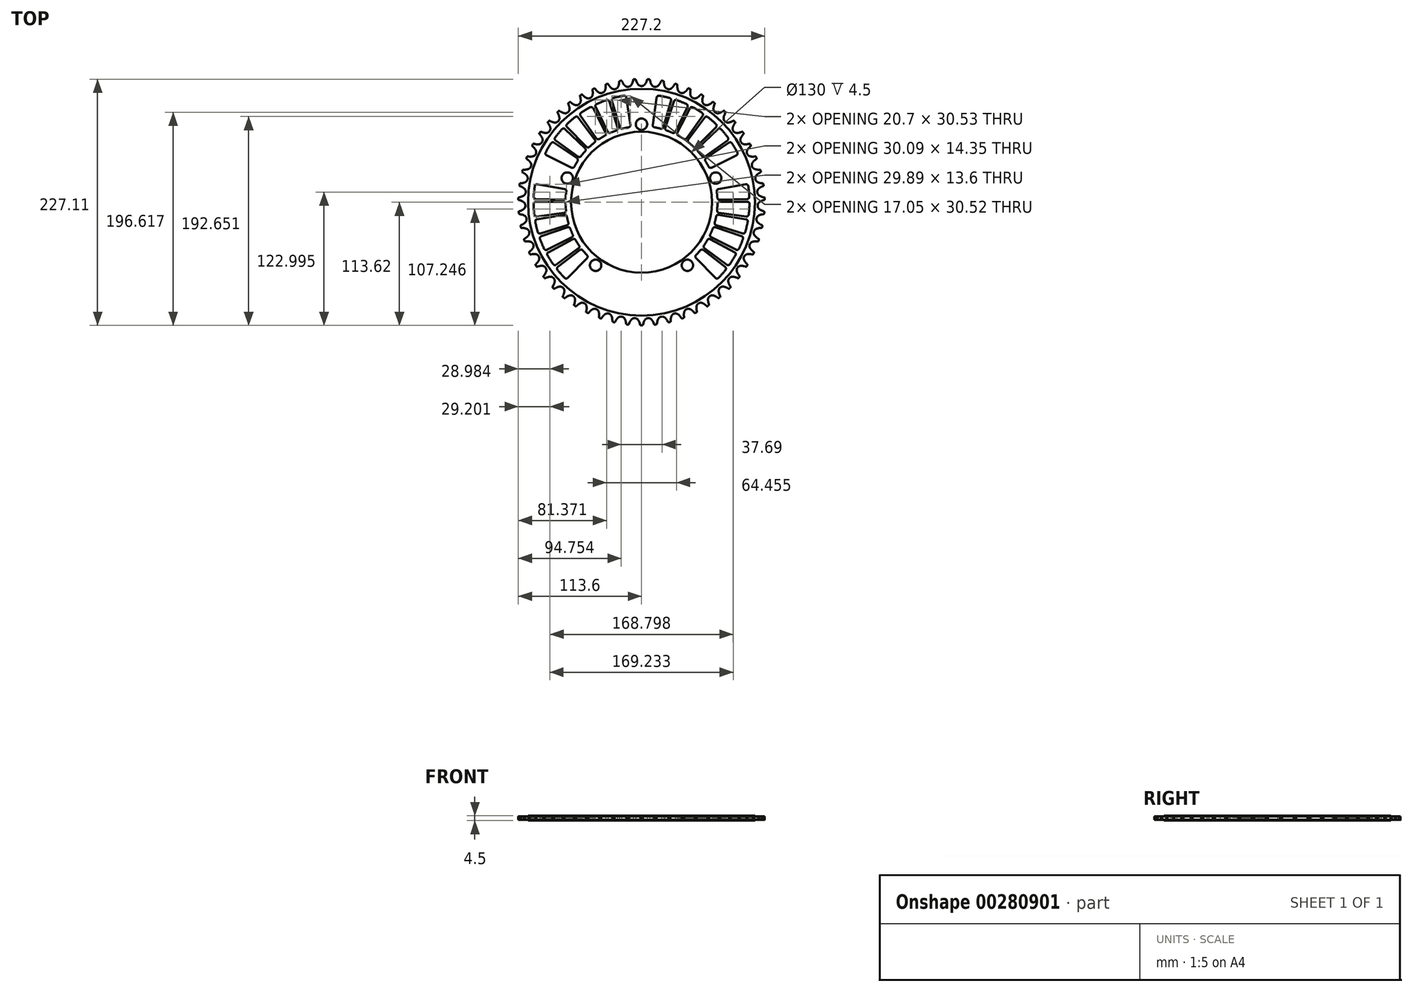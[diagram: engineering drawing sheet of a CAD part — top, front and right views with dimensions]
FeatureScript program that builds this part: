
annotation { "Feature Type Name" : "Feature", "Feature Type Description" : "" }
export const myFeature = defineFeature(function(context is Context, id is Id, definition is map)
    precondition{}
    {
        {
            var Q0;
            Q0=qCreatedBy(makeId("Top.planeOp"),FACE);
            var sketch = newSketch(context, id + "F0", { "sketchPlane" : qUnion([Q0])});
            skCircle(sketch, "E0", {"center": v(0, 0) * mm, "radius": 111.17 * mm, "construction": true});
            skArc(sketch, "E1", {"start": v(-4.68, 111.51) * mm, "mid": v(-4.06, 110.1) * mm, "end": v(-3.24, 108.8) * mm});
            skLineSegment(sketch, "E2", {"start": v(-4.68, 111.51) * mm, "end": v(-5.07, 112.63) * mm});
            skArc(sketch, "E3.trimOffspring", {"start": v(-5.07, 112.63) * mm, "mid": v(-5.69, 113.92) * mm, "end": v(-6.58, 115.05) * mm});
            skArc(sketch, "E4.trimOffspring", {"start": v(-3.24, 108.8) * mm, "mid": v(-1.82, 107.6) * mm, "end": v(0, 107.15) * mm});
            skArc(sketch, "E5.MirrorCS", {"start": v(3.24, 108.8) * mm, "mid": v(1.82, 107.6) * mm, "end": v(0, 107.15) * mm});
            skArc(sketch, "E6.MirrorCS", {"start": v(4.68, 111.51) * mm, "mid": v(4.06, 110.1) * mm, "end": v(3.24, 108.8) * mm});
            skLineSegment(sketch, "E7.MirrorCS", {"start": v(4.68, 111.51) * mm, "end": v(5.07, 112.63) * mm});
            skArc(sketch, "E8.MirrorCS", {"start": v(5.07, 112.63) * mm, "mid": v(5.69, 113.92) * mm, "end": v(6.58, 115.05) * mm});
            skArc(sketch, "E9.1.0", {"start": v(-15.63, 107.73) * mm, "mid": v(-14.07, 106.68) * mm, "end": v(-12.21, 106.46) * mm});
            skArc(sketch, "E9.1.1", {"start": v(-9.18, 108.47) * mm, "mid": v(-10.46, 107.1) * mm, "end": v(-12.21, 106.46) * mm});
            skArc(sketch, "E9.1.2", {"start": v(-8.06, 111.32) * mm, "mid": v(-8.51, 109.85) * mm, "end": v(-9.18, 108.47) * mm});
            skArc(sketch, "E9.1.3", {"start": v(-17.36, 110.25) * mm, "mid": v(-16.59, 108.93) * mm, "end": v(-15.63, 107.73) * mm});
            skArc(sketch, "E9.1.4", {"start": v(-7.8, 112.47) * mm, "mid": v(-7.34, 113.83) * mm, "end": v(-6.58, 115.05) * mm});
            skArc(sketch, "E9.1.5", {"start": v(-17.87, 111.32) * mm, "mid": v(-18.64, 112.53) * mm, "end": v(-19.65, 113.55) * mm});
            skLineSegment(sketch, "E9.1.6", {"start": v(-8.06, 111.32) * mm, "end": v(-7.8, 112.47) * mm});
            skLineSegment(sketch, "E9.1.7", {"start": v(-17.36, 110.25) * mm, "end": v(-17.87, 111.32) * mm});
            skArc(sketch, "E9.2.0", {"start": v(-27.8, 105.24) * mm, "mid": v(-26.14, 104.38) * mm, "end": v(-24.27, 104.37) * mm});
            skArc(sketch, "E9.2.1", {"start": v(-21.48, 106.71) * mm, "mid": v(-22.6, 105.2) * mm, "end": v(-24.27, 104.37) * mm});
            skArc(sketch, "E9.2.2", {"start": v(-20.7, 109.68) * mm, "mid": v(-20.98, 108.16) * mm, "end": v(-21.48, 106.71) * mm});
            skArc(sketch, "E9.2.3", {"start": v(-29.82, 107.56) * mm, "mid": v(-28.9, 106.32) * mm, "end": v(-27.8, 105.24) * mm});
            skArc(sketch, "E9.2.4", {"start": v(-20.57, 110.85) * mm, "mid": v(-20.26, 112.25) * mm, "end": v(-19.65, 113.55) * mm});
            skArc(sketch, "E9.2.5", {"start": v(-30.45, 108.55) * mm, "mid": v(-31.34, 109.68) * mm, "end": v(-32.47, 110.57) * mm});
            skLineSegment(sketch, "E9.2.6", {"start": v(-20.7, 109.68) * mm, "end": v(-20.57, 110.85) * mm});
            skLineSegment(sketch, "E9.2.7", {"start": v(-29.82, 107.56) * mm, "end": v(-30.45, 108.55) * mm});
            skArc(sketch, "E9.3.0", {"start": v(-39.62, 101.39) * mm, "mid": v(-37.87, 100.72) * mm, "end": v(-36, 100.92) * mm});
            skArc(sketch, "E9.3.1", {"start": v(-33.5, 103.57) * mm, "mid": v(-34.44, 101.95) * mm, "end": v(-36, 100.92) * mm});
            skArc(sketch, "E9.3.2", {"start": v(-33.07, 106.6) * mm, "mid": v(-33.17, 105.07) * mm, "end": v(-33.5, 103.57) * mm});
            skArc(sketch, "E9.3.3", {"start": v(-41.88, 103.46) * mm, "mid": v(-40.83, 102.34) * mm, "end": v(-39.62, 101.39) * mm});
            skArc(sketch, "E9.3.4", {"start": v(-33.08, 107.78) * mm, "mid": v(-32.93, 109.2) * mm, "end": v(-32.47, 110.57) * mm});
            skArc(sketch, "E9.3.5", {"start": v(-42.62, 104.38) * mm, "mid": v(-43.64, 105.39) * mm, "end": v(-44.86, 106.15) * mm});
            skLineSegment(sketch, "E9.3.6", {"start": v(-33.07, 106.6) * mm, "end": v(-33.08, 107.78) * mm});
            skLineSegment(sketch, "E9.3.7", {"start": v(-41.88, 103.46) * mm, "end": v(-42.62, 104.38) * mm});
            skArc(sketch, "E9.4.0", {"start": v(-50.92, 96.2) * mm, "mid": v(-49.1, 95.75) * mm, "end": v(-47.28, 96.16) * mm});
            skArc(sketch, "E9.4.1", {"start": v(-45.1, 99.07) * mm, "mid": v(-45.84, 97.35) * mm, "end": v(-47.28, 96.16) * mm});
            skArc(sketch, "E9.4.2", {"start": v(-45, 102.14) * mm, "mid": v(-44.93, 100.6) * mm, "end": v(-45.1, 99.07) * mm});
            skArc(sketch, "E9.4.3", {"start": v(-53.4, 98) * mm, "mid": v(-52.23, 97.02) * mm, "end": v(-50.92, 96.2) * mm});
            skArc(sketch, "E9.4.4", {"start": v(-45.15, 103.3) * mm, "mid": v(-45.16, 104.74) * mm, "end": v(-44.86, 106.15) * mm});
            skArc(sketch, "E9.4.5", {"start": v(-54.24, 98.84) * mm, "mid": v(-55.37, 99.73) * mm, "end": v(-56.67, 100.34) * mm});
            skLineSegment(sketch, "E9.4.6", {"start": v(-45, 102.14) * mm, "end": v(-45.15, 103.3) * mm});
            skLineSegment(sketch, "E9.4.7", {"start": v(-53.4, 98) * mm, "end": v(-54.24, 98.84) * mm});
            skArc(sketch, "E9.5.0", {"start": v(-61.55, 89.78) * mm, "mid": v(-59.7, 89.53) * mm, "end": v(-57.93, 90.14) * mm});
            skArc(sketch, "E9.5.1", {"start": v(-56.1, 93.29) * mm, "mid": v(-56.64, 91.5) * mm, "end": v(-57.93, 90.14) * mm});
            skArc(sketch, "E9.5.2", {"start": v(-56.35, 96.34) * mm, "mid": v(-56.1, 94.82) * mm, "end": v(-56.1, 93.29) * mm});
            skArc(sketch, "E9.5.3", {"start": v(-64.23, 91.28) * mm, "mid": v(-62.95, 90.43) * mm, "end": v(-61.55, 89.78) * mm});
            skArc(sketch, "E9.5.4", {"start": v(-56.63, 97.49) * mm, "mid": v(-56.8, 98.91) * mm, "end": v(-56.67, 100.34) * mm});
            skArc(sketch, "E9.5.5", {"start": v(-65.15, 92) * mm, "mid": v(-66.38, 92.76) * mm, "end": v(-67.73, 93.23) * mm});
            skLineSegment(sketch, "E9.5.6", {"start": v(-56.35, 96.34) * mm, "end": v(-56.63, 97.49) * mm});
            skLineSegment(sketch, "E9.5.7", {"start": v(-64.23, 91.28) * mm, "end": v(-65.15, 92) * mm});
            skArc(sketch, "E9.6.0", {"start": v(-71.39, 82.18) * mm, "mid": v(-69.52, 82.14) * mm, "end": v(-67.83, 82.95) * mm});
            skArc(sketch, "E9.6.1", {"start": v(-66.36, 86.28) * mm, "mid": v(-66.7, 84.44) * mm, "end": v(-67.83, 82.95) * mm});
            skArc(sketch, "E9.6.2", {"start": v(-66.97, 89.3) * mm, "mid": v(-66.55, 87.8) * mm, "end": v(-66.36, 86.28) * mm});
            skArc(sketch, "E9.6.3", {"start": v(-74.21, 83.36) * mm, "mid": v(-72.84, 82.67) * mm, "end": v(-71.39, 82.18) * mm});
            skArc(sketch, "E9.6.4", {"start": v(-67.37, 90.4) * mm, "mid": v(-67.71, 91.8) * mm, "end": v(-67.73, 93.23) * mm});
            skArc(sketch, "E9.6.5", {"start": v(-75.22, 83.98) * mm, "mid": v(-76.52, 84.6) * mm, "end": v(-77.92, 84.9) * mm});
            skLineSegment(sketch, "E9.6.6", {"start": v(-66.97, 89.3) * mm, "end": v(-67.37, 90.4) * mm});
            skLineSegment(sketch, "E9.6.7", {"start": v(-74.21, 83.36) * mm, "end": v(-75.22, 83.98) * mm});
            skArc(sketch, "E9.7.0", {"start": v(-80.29, 73.5) * mm, "mid": v(-78.43, 73.68) * mm, "end": v(-76.84, 74.68) * mm});
            skArc(sketch, "E9.7.1", {"start": v(-75.77, 78.16) * mm, "mid": v(-75.89, 76.29) * mm, "end": v(-76.84, 74.68) * mm});
            skArc(sketch, "E9.7.2", {"start": v(-76.7, 81.08) * mm, "mid": v(-76.13, 79.65) * mm, "end": v(-75.77, 78.16) * mm});
            skArc(sketch, "E9.7.3", {"start": v(-83.23, 74.36) * mm, "mid": v(-81.8, 73.82) * mm, "end": v(-80.29, 73.5) * mm});
            skArc(sketch, "E9.7.4", {"start": v(-77.24, 82.13) * mm, "mid": v(-77.74, 83.48) * mm, "end": v(-77.92, 84.9) * mm});
            skArc(sketch, "E9.7.5", {"start": v(-84.3, 74.86) * mm, "mid": v(-85.66, 75.32) * mm, "end": v(-87.09, 75.46) * mm});
            skLineSegment(sketch, "E9.7.6", {"start": v(-76.7, 81.08) * mm, "end": v(-77.24, 82.13) * mm});
            skLineSegment(sketch, "E9.7.7", {"start": v(-83.23, 74.36) * mm, "end": v(-84.3, 74.86) * mm});
            skArc(sketch, "E9.8.0", {"start": v(-88.14, 63.87) * mm, "mid": v(-86.31, 64.26) * mm, "end": v(-84.86, 65.43) * mm});
            skArc(sketch, "E9.8.1", {"start": v(-84.18, 69.01) * mm, "mid": v(-84.09, 67.14) * mm, "end": v(-84.86, 65.43) * mm});
            skArc(sketch, "E9.8.2", {"start": v(-85.45, 71.8) * mm, "mid": v(-84.71, 70.45) * mm, "end": v(-84.18, 69.01) * mm});
            skArc(sketch, "E9.8.3", {"start": v(-91.17, 64.39) * mm, "mid": v(-89.67, 64.02) * mm, "end": v(-88.14, 63.87) * mm});
            skArc(sketch, "E9.8.4", {"start": v(-86.1, 72.79) * mm, "mid": v(-86.74, 74.07) * mm, "end": v(-87.09, 75.46) * mm});
            skArc(sketch, "E9.8.5", {"start": v(-92.29, 64.76) * mm, "mid": v(-93.69, 65.06) * mm, "end": v(-95.12, 65.04) * mm});
            skLineSegment(sketch, "E9.8.6", {"start": v(-85.45, 71.8) * mm, "end": v(-86.1, 72.79) * mm});
            skLineSegment(sketch, "E9.8.7", {"start": v(-91.17, 64.39) * mm, "end": v(-92.29, 64.76) * mm});
            skArc(sketch, "E9.9.0", {"start": v(-94.85, 53.4) * mm, "mid": v(-93.08, 54) * mm, "end": v(-91.76, 55.33) * mm});
            skArc(sketch, "E9.9.1", {"start": v(-91.5, 58.96) * mm, "mid": v(-91.2, 57.12) * mm, "end": v(-91.76, 55.33) * mm});
            skArc(sketch, "E9.9.2", {"start": v(-93.08, 61.6) * mm, "mid": v(-92.2, 60.34) * mm, "end": v(-91.5, 58.96) * mm});
            skArc(sketch, "E9.9.3", {"start": v(-97.91, 53.58) * mm, "mid": v(-96.39, 53.38) * mm, "end": v(-94.85, 53.4) * mm});
            skArc(sketch, "E9.9.4", {"start": v(-93.83, 62.5) * mm, "mid": v(-94.62, 63.7) * mm, "end": v(-95.12, 65.04) * mm});
            skArc(sketch, "E9.9.5", {"start": v(-99.07, 53.82) * mm, "mid": v(-100.5, 53.96) * mm, "end": v(-101.92, 53.78) * mm});
            skLineSegment(sketch, "E9.9.6", {"start": v(-93.08, 61.6) * mm, "end": v(-93.83, 62.5) * mm});
            skLineSegment(sketch, "E9.9.7", {"start": v(-97.91, 53.58) * mm, "end": v(-99.07, 53.82) * mm});
            skArc(sketch, "E9.10.0", {"start": v(-100.32, 42.25) * mm, "mid": v(-98.62, 43.04) * mm, "end": v(-97.47, 44.51) * mm});
            skArc(sketch, "E9.10.1", {"start": v(-97.62, 48.15) * mm, "mid": v(-97.11, 46.35) * mm, "end": v(-97.47, 44.51) * mm});
            skArc(sketch, "E9.10.2", {"start": v(-99.5, 50.58) * mm, "mid": v(-98.47, 49.44) * mm, "end": v(-97.62, 48.15) * mm});
            skArc(sketch, "E9.10.3", {"start": v(-103.38, 42.07) * mm, "mid": v(-101.84, 42.04) * mm, "end": v(-100.32, 42.25) * mm});
            skArc(sketch, "E9.10.4", {"start": v(-100.35, 51.4) * mm, "mid": v(-101.27, 52.5) * mm, "end": v(-101.92, 53.78) * mm});
            skArc(sketch, "E9.10.5", {"start": v(-104.56, 42.18) * mm, "mid": v(-106, 42.15) * mm, "end": v(-107.38, 41.8) * mm});
            skLineSegment(sketch, "E9.10.6", {"start": v(-99.5, 50.58) * mm, "end": v(-100.35, 51.4) * mm});
            skLineSegment(sketch, "E9.10.7", {"start": v(-103.38, 42.07) * mm, "end": v(-104.56, 42.18) * mm});
            skArc(sketch, "E9.11.0", {"start": v(-104.48, 30.54) * mm, "mid": v(-102.89, 31.52) * mm, "end": v(-101.91, 33.11) * mm});
            skArc(sketch, "E9.11.1", {"start": v(-102.48, 36.7) * mm, "mid": v(-101.76, 34.98) * mm, "end": v(-101.91, 33.11) * mm});
            skArc(sketch, "E9.11.2", {"start": v(-104.6, 38.91) * mm, "mid": v(-103.46, 37.89) * mm, "end": v(-102.48, 36.7) * mm});
            skArc(sketch, "E9.11.3", {"start": v(-107.5, 30) * mm, "mid": v(-105.97, 30.16) * mm, "end": v(-104.48, 30.54) * mm});
            skArc(sketch, "E9.11.4", {"start": v(-105.55, 39.62) * mm, "mid": v(-106.6, 40.61) * mm, "end": v(-107.38, 41.8) * mm});
            skArc(sketch, "E9.11.5", {"start": v(-108.68, 29.98) * mm, "mid": v(-110.1, 29.8) * mm, "end": v(-111.45, 29.3) * mm});
            skLineSegment(sketch, "E9.11.6", {"start": v(-104.6, 38.91) * mm, "end": v(-105.55, 39.62) * mm});
            skLineSegment(sketch, "E9.11.7", {"start": v(-107.5, 30) * mm, "end": v(-108.68, 29.98) * mm});
            skArc(sketch, "E9.12.0", {"start": v(-107.28, 18.43) * mm, "mid": v(-105.8, 19.58) * mm, "end": v(-105.02, 21.28) * mm});
            skArc(sketch, "E9.12.1", {"start": v(-106, 24.79) * mm, "mid": v(-105.09, 23.15) * mm, "end": v(-105.02, 21.28) * mm});
            skArc(sketch, "E9.12.2", {"start": v(-108.36, 26.73) * mm, "mid": v(-107.1, 25.85) * mm, "end": v(-106, 24.79) * mm});
            skArc(sketch, "E9.12.3", {"start": v(-110.22, 17.56) * mm, "mid": v(-108.72, 17.88) * mm, "end": v(-107.28, 18.43) * mm});
            skArc(sketch, "E9.12.4", {"start": v(-109.38, 27.33) * mm, "mid": v(-110.53, 28.2) * mm, "end": v(-111.45, 29.3) * mm});
            skArc(sketch, "E9.12.5", {"start": v(-111.4, 17.4) * mm, "mid": v(-112.78, 17.05) * mm, "end": v(-114.06, 16.4) * mm});
            skLineSegment(sketch, "E9.12.6", {"start": v(-108.36, 26.73) * mm, "end": v(-109.38, 27.33) * mm});
            skLineSegment(sketch, "E9.12.7", {"start": v(-110.22, 17.56) * mm, "end": v(-111.4, 17.4) * mm});
            skArc(sketch, "E9.13.0", {"start": v(-108.68, 6.08) * mm, "mid": v(-107.35, 7.4) * mm, "end": v(-106.76, 9.17) * mm});
            skArc(sketch, "E9.13.1", {"start": v(-108.13, 12.54) * mm, "mid": v(-107.04, 11.02) * mm, "end": v(-106.76, 9.17) * mm});
            skArc(sketch, "E9.13.2", {"start": v(-110.7, 14.2) * mm, "mid": v(-109.35, 13.47) * mm, "end": v(-108.13, 12.54) * mm});
            skArc(sketch, "E9.13.3", {"start": v(-111.5, 4.88) * mm, "mid": v(-110.05, 5.37) * mm, "end": v(-108.68, 6.08) * mm});
            skArc(sketch, "E9.13.4", {"start": v(-111.78, 14.69) * mm, "mid": v(-113.02, 15.41) * mm, "end": v(-114.06, 16.4) * mm});
            skArc(sketch, "E9.13.5", {"start": v(-112.65, 4.59) * mm, "mid": v(-114, 4.08) * mm, "end": v(-115.19, 3.3) * mm});
            skLineSegment(sketch, "E9.13.6", {"start": v(-110.7, 14.2) * mm, "end": v(-111.78, 14.69) * mm});
            skLineSegment(sketch, "E9.13.7", {"start": v(-111.5, 4.88) * mm, "end": v(-112.65, 4.59) * mm});
            skArc(sketch, "E9.14.0", {"start": v(-108.67, -6.35) * mm, "mid": v(-107.5, -4.9) * mm, "end": v(-107.11, -3.06) * mm});
            skArc(sketch, "E9.14.1", {"start": v(-108.85, 0.14) * mm, "mid": v(-107.6, -1.25) * mm, "end": v(-107.11, -3.06) * mm});
            skArc(sketch, "E9.14.2", {"start": v(-111.6, 1.5) * mm, "mid": v(-110.18, 0.92) * mm, "end": v(-108.85, 0.14) * mm});
            skArc(sketch, "E9.14.3", {"start": v(-111.33, -7.86) * mm, "mid": v(-109.94, -7.2) * mm, "end": v(-108.67, -6.35) * mm});
            skArc(sketch, "E9.14.4", {"start": v(-112.73, 1.85) * mm, "mid": v(-114.04, 2.43) * mm, "end": v(-115.19, 3.3) * mm});
            skArc(sketch, "E9.14.5", {"start": v(-112.44, -8.28) * mm, "mid": v(-113.71, -8.94) * mm, "end": v(-114.81, -9.86) * mm});
            skLineSegment(sketch, "E9.14.6", {"start": v(-111.6, 1.5) * mm, "end": v(-112.73, 1.85) * mm});
            skLineSegment(sketch, "E9.14.7", {"start": v(-111.33, -7.86) * mm, "end": v(-112.44, -8.28) * mm});
            skArc(sketch, "E9.15.0", {"start": v(-107.24, -18.7) * mm, "mid": v(-106.24, -17.11) * mm, "end": v(-106.06, -15.25) * mm});
            skArc(sketch, "E9.15.1", {"start": v(-108.16, -12.27) * mm, "mid": v(-106.75, -13.51) * mm, "end": v(-106.06, -15.25) * mm});
            skArc(sketch, "E9.15.2", {"start": v(-111.05, -11.24) * mm, "mid": v(-109.56, -11.65) * mm, "end": v(-108.16, -12.27) * mm});
            skArc(sketch, "E9.15.3", {"start": v(-109.71, -20.5) * mm, "mid": v(-108.4, -19.7) * mm, "end": v(-107.24, -18.7) * mm});
            skArc(sketch, "E9.15.4", {"start": v(-112.2, -11.01) * mm, "mid": v(-113.57, -10.58) * mm, "end": v(-114.81, -9.86) * mm});
            skArc(sketch, "E9.15.5", {"start": v(-110.76, -21.04) * mm, "mid": v(-111.95, -21.84) * mm, "end": v(-112.94, -22.88) * mm});
            skLineSegment(sketch, "E9.15.6", {"start": v(-111.05, -11.24) * mm, "end": v(-112.2, -11.01) * mm});
            skLineSegment(sketch, "E9.15.7", {"start": v(-109.71, -20.5) * mm, "end": v(-110.76, -21.04) * mm});
            skArc(sketch, "E9.16.0", {"start": v(-104.4, -30.8) * mm, "mid": v(-103.6, -29.11) * mm, "end": v(-103.63, -27.24) * mm});
            skArc(sketch, "E9.16.1", {"start": v(-106.05, -24.52) * mm, "mid": v(-104.52, -25.6) * mm, "end": v(-103.63, -27.24) * mm});
            skArc(sketch, "E9.16.2", {"start": v(-109.04, -23.82) * mm, "mid": v(-107.52, -24.06) * mm, "end": v(-106.05, -24.52) * mm});
            skArc(sketch, "E9.16.3", {"start": v(-106.66, -32.88) * mm, "mid": v(-105.46, -31.92) * mm, "end": v(-104.4, -30.8) * mm});
            skArc(sketch, "E9.16.4", {"start": v(-110.22, -23.73) * mm, "mid": v(-111.63, -23.46) * mm, "end": v(-112.94, -22.88) * mm});
            skArc(sketch, "E9.16.5", {"start": v(-107.64, -33.53) * mm, "mid": v(-108.74, -34.46) * mm, "end": v(-109.6, -35.6) * mm});
            skLineSegment(sketch, "E9.16.6", {"start": v(-109.04, -23.82) * mm, "end": v(-110.22, -23.73) * mm});
            skLineSegment(sketch, "E9.16.7", {"start": v(-106.66, -32.88) * mm, "end": v(-107.64, -33.53) * mm});
            skArc(sketch, "E9.17.0", {"start": v(-100.21, -42.5) * mm, "mid": v(-99.6, -40.73) * mm, "end": v(-99.85, -38.88) * mm});
            skArc(sketch, "E9.17.1", {"start": v(-102.57, -36.45) * mm, "mid": v(-100.92, -37.34) * mm, "end": v(-99.85, -38.88) * mm});
            skArc(sketch, "E9.17.2", {"start": v(-105.61, -36.1) * mm, "mid": v(-104.08, -36.16) * mm, "end": v(-102.57, -36.45) * mm});
            skArc(sketch, "E9.17.3", {"start": v(-102.22, -44.82) * mm, "mid": v(-101.13, -43.73) * mm, "end": v(-100.21, -42.5) * mm});
            skArc(sketch, "E9.17.4", {"start": v(-106.8, -36.14) * mm, "mid": v(-108.22, -36.03) * mm, "end": v(-109.6, -35.6) * mm});
            skArc(sketch, "E9.17.5", {"start": v(-103.12, -45.58) * mm, "mid": v(-104.1, -46.63) * mm, "end": v(-104.82, -47.87) * mm});
            skLineSegment(sketch, "E9.17.6", {"start": v(-105.61, -36.1) * mm, "end": v(-106.8, -36.14) * mm});
            skLineSegment(sketch, "E9.17.7", {"start": v(-102.22, -44.82) * mm, "end": v(-103.12, -45.58) * mm});
            skArc(sketch, "E9.18.0", {"start": v(-94.72, -53.65) * mm, "mid": v(-94.3, -51.82) * mm, "end": v(-94.77, -50) * mm});
            skArc(sketch, "E9.18.1", {"start": v(-97.74, -47.9) * mm, "mid": v(-96, -48.6) * mm, "end": v(-94.77, -50) * mm});
            skArc(sketch, "E9.18.2", {"start": v(-100.81, -47.9) * mm, "mid": v(-99.28, -47.79) * mm, "end": v(-97.74, -47.9) * mm});
            skArc(sketch, "E9.18.3", {"start": v(-96.44, -56.18) * mm, "mid": v(-95.49, -54.98) * mm, "end": v(-94.72, -53.65) * mm});
            skArc(sketch, "E9.18.4", {"start": v(-101.98, -48.08) * mm, "mid": v(-103.41, -48.14) * mm, "end": v(-104.82, -47.87) * mm});
            skArc(sketch, "E9.18.5", {"start": v(-97.25, -57.04) * mm, "mid": v(-98.1, -58.2) * mm, "end": v(-98.68, -59.5) * mm});
            skLineSegment(sketch, "E9.18.6", {"start": v(-100.81, -47.9) * mm, "end": v(-101.98, -48.08) * mm});
            skLineSegment(sketch, "E9.18.7", {"start": v(-96.44, -56.18) * mm, "end": v(-97.25, -57.04) * mm});
            skArc(sketch, "E9.19.0", {"start": v(-87.98, -64.1) * mm, "mid": v(-87.79, -62.23) * mm, "end": v(-88.45, -60.48) * mm});
            skArc(sketch, "E9.19.1", {"start": v(-91.65, -58.74) * mm, "mid": v(-89.84, -59.23) * mm, "end": v(-88.45, -60.48) * mm});
            skArc(sketch, "E9.19.2", {"start": v(-94.7, -59.08) * mm, "mid": v(-93.18, -58.8) * mm, "end": v(-91.65, -58.74) * mm});
            skArc(sketch, "E9.19.3", {"start": v(-89.4, -66.8) * mm, "mid": v(-88.6, -65.5) * mm, "end": v(-87.98, -64.1) * mm});
            skArc(sketch, "E9.19.4", {"start": v(-95.83, -59.39) * mm, "mid": v(-97.25, -59.6) * mm, "end": v(-98.68, -59.5) * mm});
            skArc(sketch, "E9.19.5", {"start": v(-90.11, -67.76) * mm, "mid": v(-90.83, -69) * mm, "end": v(-91.26, -70.37) * mm});
            skLineSegment(sketch, "E9.19.6", {"start": v(-94.7, -59.08) * mm, "end": v(-95.83, -59.39) * mm});
            skLineSegment(sketch, "E9.19.7", {"start": v(-89.4, -66.8) * mm, "end": v(-90.11, -67.76) * mm});
            skArc(sketch, "E9.20.0", {"start": v(-80.1, -73.7) * mm, "mid": v(-80.12, -71.83) * mm, "end": v(-80.98, -70.17) * mm});
            skArc(sketch, "E9.20.1", {"start": v(-84.35, -68.8) * mm, "mid": v(-82.5, -69.08) * mm, "end": v(-80.98, -70.17) * mm});
            skArc(sketch, "E9.20.2", {"start": v(-87.34, -69.49) * mm, "mid": v(-85.87, -69.03) * mm, "end": v(-84.35, -68.8) * mm});
            skArc(sketch, "E9.20.3", {"start": v(-81.21, -76.56) * mm, "mid": v(-80.55, -75.17) * mm, "end": v(-80.1, -73.7) * mm});
            skArc(sketch, "E9.20.4", {"start": v(-88.44, -69.93) * mm, "mid": v(-89.82, -70.3) * mm, "end": v(-91.26, -70.37) * mm});
            skArc(sketch, "E9.20.5", {"start": v(-81.8, -77.59) * mm, "mid": v(-82.37, -78.9) * mm, "end": v(-82.64, -80.31) * mm});
            skLineSegment(sketch, "E9.20.6", {"start": v(-87.34, -69.49) * mm, "end": v(-88.44, -69.93) * mm});
            skLineSegment(sketch, "E9.20.7", {"start": v(-81.21, -76.56) * mm, "end": v(-81.8, -77.59) * mm});
            skArc(sketch, "E9.21.0", {"start": v(-71.18, -82.35) * mm, "mid": v(-71.4, -80.5) * mm, "end": v(-72.46, -78.95) * mm});
            skArc(sketch, "E9.21.1", {"start": v(-75.96, -77.97) * mm, "mid": v(-74.1, -78.04) * mm, "end": v(-72.46, -78.95) * mm});
            skArc(sketch, "E9.21.2", {"start": v(-78.85, -79) * mm, "mid": v(-77.44, -78.37) * mm, "end": v(-75.96, -77.97) * mm});
            skArc(sketch, "E9.21.3", {"start": v(-71.95, -85.32) * mm, "mid": v(-71.46, -83.87) * mm, "end": v(-71.18, -82.35) * mm});
            skArc(sketch, "E9.21.4", {"start": v(-79.89, -79.55) * mm, "mid": v(-81.22, -80.09) * mm, "end": v(-82.64, -80.31) * mm});
            skArc(sketch, "E9.21.5", {"start": v(-72.42, -86.4) * mm, "mid": v(-72.84, -87.78) * mm, "end": v(-72.95, -89.2) * mm});
            skLineSegment(sketch, "E9.21.6", {"start": v(-78.85, -79) * mm, "end": v(-79.89, -79.55) * mm});
            skLineSegment(sketch, "E9.21.7", {"start": v(-71.95, -85.32) * mm, "end": v(-72.42, -86.4) * mm});
            skArc(sketch, "E9.22.0", {"start": v(-61.33, -89.93) * mm, "mid": v(-61.77, -88.11) * mm, "end": v(-62.98, -86.69) * mm});
            skArc(sketch, "E9.22.1", {"start": v(-66.58, -86.12) * mm, "mid": v(-64.71, -85.97) * mm, "end": v(-62.98, -86.69) * mm});
            skArc(sketch, "E9.22.2", {"start": v(-69.33, -87.47) * mm, "mid": v(-68, -86.69) * mm, "end": v(-66.58, -86.12) * mm});
            skArc(sketch, "E9.22.3", {"start": v(-61.76, -92.97) * mm, "mid": v(-61.43, -91.47) * mm, "end": v(-61.33, -89.93) * mm});
            skArc(sketch, "E9.22.4", {"start": v(-70.3, -88.14) * mm, "mid": v(-71.56, -88.82) * mm, "end": v(-72.95, -89.2) * mm});
            skArc(sketch, "E9.22.5", {"start": v(-62.1, -94.1) * mm, "mid": v(-62.36, -95.5) * mm, "end": v(-62.3, -96.94) * mm});
            skLineSegment(sketch, "E9.22.6", {"start": v(-69.33, -87.47) * mm, "end": v(-70.3, -88.14) * mm});
            skLineSegment(sketch, "E9.22.7", {"start": v(-61.76, -92.97) * mm, "end": v(-62.1, -94.1) * mm});
            skArc(sketch, "E9.23.0", {"start": v(-50.68, -96.34) * mm, "mid": v(-51.32, -94.58) * mm, "end": v(-52.7, -93.3) * mm});
            skArc(sketch, "E9.23.1", {"start": v(-56.33, -93.15) * mm, "mid": v(-54.5, -92.79) * mm, "end": v(-52.7, -93.3) * mm});
            skArc(sketch, "E9.23.2", {"start": v(-58.91, -94.8) * mm, "mid": v(-57.68, -93.88) * mm, "end": v(-56.33, -93.15) * mm});
            skArc(sketch, "E9.23.3", {"start": v(-50.76, -99.4) * mm, "mid": v(-50.6, -97.87) * mm, "end": v(-50.68, -96.34) * mm});
            skArc(sketch, "E9.23.4", {"start": v(-59.8, -95.58) * mm, "mid": v(-60.97, -96.4) * mm, "end": v(-62.3, -96.94) * mm});
            skArc(sketch, "E9.23.5", {"start": v(-50.97, -100.56) * mm, "mid": v(-51.07, -102) * mm, "end": v(-50.84, -103.41) * mm});
            skLineSegment(sketch, "E9.23.6", {"start": v(-58.91, -94.8) * mm, "end": v(-59.8, -95.58) * mm});
            skLineSegment(sketch, "E9.23.7", {"start": v(-50.76, -99.4) * mm, "end": v(-50.97, -100.56) * mm});
            skArc(sketch, "E9.24.0", {"start": v(-39.37, -101.49) * mm, "mid": v(-40.2, -99.81) * mm, "end": v(-41.71, -98.7) * mm});
            skArc(sketch, "E9.24.1", {"start": v(-45.34, -98.96) * mm, "mid": v(-43.56, -98.4) * mm, "end": v(-41.71, -98.7) * mm});
            skArc(sketch, "E9.24.2", {"start": v(-47.72, -100.9) * mm, "mid": v(-46.6, -99.84) * mm, "end": v(-45.34, -98.96) * mm});
            skArc(sketch, "E9.24.3", {"start": v(-39.1, -104.54) * mm, "mid": v(-39.12, -103) * mm, "end": v(-39.37, -101.49) * mm});
            skArc(sketch, "E9.24.4", {"start": v(-48.51, -101.77) * mm, "mid": v(-49.58, -102.72) * mm, "end": v(-50.84, -103.41) * mm});
            skArc(sketch, "E9.24.5", {"start": v(-39.18, -105.72) * mm, "mid": v(-39.1, -107.15) * mm, "end": v(-38.73, -108.53) * mm});
            skLineSegment(sketch, "E9.24.6", {"start": v(-47.72, -100.9) * mm, "end": v(-48.51, -101.77) * mm});
            skLineSegment(sketch, "E9.24.7", {"start": v(-39.1, -104.54) * mm, "end": v(-39.18, -105.72) * mm});
            skArc(sketch, "E9.25.0", {"start": v(-27.54, -105.31) * mm, "mid": v(-28.57, -103.75) * mm, "end": v(-30.19, -102.81) * mm});
            skArc(sketch, "E9.25.1", {"start": v(-33.77, -103.48) * mm, "mid": v(-32.06, -102.72) * mm, "end": v(-30.19, -102.81) * mm});
            skArc(sketch, "E9.25.2", {"start": v(-35.9, -105.68) * mm, "mid": v(-34.92, -104.5) * mm, "end": v(-33.77, -103.48) * mm});
            skArc(sketch, "E9.25.3", {"start": v(-26.93, -108.32) * mm, "mid": v(-27.12, -106.8) * mm, "end": v(-27.54, -105.31) * mm});
            skArc(sketch, "E9.25.4", {"start": v(-36.6, -106.64) * mm, "mid": v(-37.55, -107.7) * mm, "end": v(-38.73, -108.53) * mm});
            skArc(sketch, "E9.25.5", {"start": v(-26.87, -109.5) * mm, "mid": v(-26.64, -110.91) * mm, "end": v(-26.1, -112.24) * mm});
            skLineSegment(sketch, "E9.25.6", {"start": v(-35.9, -105.68) * mm, "end": v(-36.6, -106.64) * mm});
            skLineSegment(sketch, "E9.25.7", {"start": v(-26.93, -108.32) * mm, "end": v(-26.87, -109.5) * mm});
            skArc(sketch, "E9.26.0", {"start": v(-15.36, -107.76) * mm, "mid": v(-16.55, -106.33) * mm, "end": v(-18.27, -105.59) * mm});
            skArc(sketch, "E9.26.1", {"start": v(-21.75, -106.66) * mm, "mid": v(-20.14, -105.7) * mm, "end": v(-18.27, -105.59) * mm});
            skArc(sketch, "E9.26.2", {"start": v(-23.63, -109.08) * mm, "mid": v(-22.78, -107.8) * mm, "end": v(-21.75, -106.66) * mm});
            skArc(sketch, "E9.26.3", {"start": v(-14.4, -110.68) * mm, "mid": v(-14.77, -109.19) * mm, "end": v(-15.36, -107.76) * mm});
            skArc(sketch, "E9.26.4", {"start": v(-24.2, -110.11) * mm, "mid": v(-25.03, -111.29) * mm, "end": v(-26.1, -112.24) * mm});
            skArc(sketch, "E9.26.5", {"start": v(-14.21, -111.84) * mm, "mid": v(-13.82, -113.22) * mm, "end": v(-13.14, -114.48) * mm});
            skLineSegment(sketch, "E9.26.6", {"start": v(-23.63, -109.08) * mm, "end": v(-24.2, -110.11) * mm});
            skLineSegment(sketch, "E9.26.7", {"start": v(-14.4, -110.68) * mm, "end": v(-14.21, -111.84) * mm});
            skArc(sketch, "E9.27.0", {"start": v(-2.97, -108.81) * mm, "mid": v(-4.33, -107.52) * mm, "end": v(-6.12, -106.98) * mm});
            skArc(sketch, "E9.27.1", {"start": v(-9.45, -108.44) * mm, "mid": v(-7.96, -107.31) * mm, "end": v(-6.12, -106.98) * mm});
            skArc(sketch, "E9.27.2", {"start": v(-11.04, -111.06) * mm, "mid": v(-10.34, -109.7) * mm, "end": v(-9.45, -108.44) * mm});
            skArc(sketch, "E9.27.3", {"start": v(-1.7, -111.6) * mm, "mid": v(-2.23, -110.16) * mm, "end": v(-2.97, -108.81) * mm});
            skArc(sketch, "E9.27.4", {"start": v(-11.49, -112.16) * mm, "mid": v(-12.18, -113.41) * mm, "end": v(-13.14, -114.48) * mm});
            skArc(sketch, "E9.27.5", {"start": v(-1.37, -112.73) * mm, "mid": v(-0.83, -114.06) * mm, "end": v(0, -115.24) * mm});
            skLineSegment(sketch, "E9.27.6", {"start": v(-11.04, -111.06) * mm, "end": v(-11.49, -112.16) * mm});
            skLineSegment(sketch, "E9.27.7", {"start": v(-1.7, -111.6) * mm, "end": v(-1.37, -112.73) * mm});
            skArc(sketch, "E9.28.0", {"start": v(9.45, -108.44) * mm, "mid": v(7.96, -107.31) * mm, "end": v(6.12, -106.98) * mm});
            skArc(sketch, "E9.28.1", {"start": v(2.97, -108.81) * mm, "mid": v(4.33, -107.52) * mm, "end": v(6.12, -106.98) * mm});
            skArc(sketch, "E9.28.2", {"start": v(1.7, -111.6) * mm, "mid": v(2.23, -110.16) * mm, "end": v(2.97, -108.81) * mm});
            skArc(sketch, "E9.28.3", {"start": v(11.04, -111.06) * mm, "mid": v(10.34, -109.7) * mm, "end": v(9.45, -108.44) * mm});
            skArc(sketch, "E9.28.4", {"start": v(1.37, -112.73) * mm, "mid": v(0.83, -114.06) * mm, "end": v(0, -115.24) * mm});
            skArc(sketch, "E9.28.5", {"start": v(11.49, -112.16) * mm, "mid": v(12.18, -113.41) * mm, "end": v(13.14, -114.48) * mm});
            skLineSegment(sketch, "E9.28.6", {"start": v(1.7, -111.6) * mm, "end": v(1.37, -112.73) * mm});
            skLineSegment(sketch, "E9.28.7", {"start": v(11.04, -111.06) * mm, "end": v(11.49, -112.16) * mm});
            skArc(sketch, "E9.29.0", {"start": v(21.75, -106.66) * mm, "mid": v(20.14, -105.7) * mm, "end": v(18.27, -105.59) * mm});
            skArc(sketch, "E9.29.1", {"start": v(15.36, -107.76) * mm, "mid": v(16.55, -106.33) * mm, "end": v(18.27, -105.59) * mm});
            skArc(sketch, "E9.29.2", {"start": v(14.4, -110.68) * mm, "mid": v(14.77, -109.19) * mm, "end": v(15.36, -107.76) * mm});
            skArc(sketch, "E9.29.3", {"start": v(23.63, -109.08) * mm, "mid": v(22.78, -107.8) * mm, "end": v(21.75, -106.66) * mm});
            skArc(sketch, "E9.29.4", {"start": v(14.21, -111.84) * mm, "mid": v(13.82, -113.22) * mm, "end": v(13.14, -114.48) * mm});
            skArc(sketch, "E9.29.5", {"start": v(24.2, -110.11) * mm, "mid": v(25.03, -111.29) * mm, "end": v(26.1, -112.24) * mm});
            skLineSegment(sketch, "E9.29.6", {"start": v(14.4, -110.68) * mm, "end": v(14.21, -111.84) * mm});
            skLineSegment(sketch, "E9.29.7", {"start": v(23.63, -109.08) * mm, "end": v(24.2, -110.11) * mm});
            skArc(sketch, "E9.30.0", {"start": v(33.77, -103.48) * mm, "mid": v(32.06, -102.72) * mm, "end": v(30.19, -102.81) * mm});
            skArc(sketch, "E9.30.1", {"start": v(27.54, -105.31) * mm, "mid": v(28.57, -103.75) * mm, "end": v(30.19, -102.81) * mm});
            skArc(sketch, "E9.30.2", {"start": v(26.93, -108.32) * mm, "mid": v(27.12, -106.8) * mm, "end": v(27.54, -105.31) * mm});
            skArc(sketch, "E9.30.3", {"start": v(35.9, -105.68) * mm, "mid": v(34.92, -104.5) * mm, "end": v(33.77, -103.48) * mm});
            skArc(sketch, "E9.30.4", {"start": v(26.87, -109.5) * mm, "mid": v(26.64, -110.91) * mm, "end": v(26.1, -112.24) * mm});
            skArc(sketch, "E9.30.5", {"start": v(36.6, -106.64) * mm, "mid": v(37.55, -107.7) * mm, "end": v(38.73, -108.53) * mm});
            skLineSegment(sketch, "E9.30.6", {"start": v(26.93, -108.32) * mm, "end": v(26.87, -109.5) * mm});
            skLineSegment(sketch, "E9.30.7", {"start": v(35.9, -105.68) * mm, "end": v(36.6, -106.64) * mm});
            skArc(sketch, "E9.31.0", {"start": v(45.34, -98.96) * mm, "mid": v(43.56, -98.4) * mm, "end": v(41.71, -98.7) * mm});
            skArc(sketch, "E9.31.1", {"start": v(39.37, -101.49) * mm, "mid": v(40.2, -99.81) * mm, "end": v(41.71, -98.7) * mm});
            skArc(sketch, "E9.31.2", {"start": v(39.1, -104.54) * mm, "mid": v(39.12, -103) * mm, "end": v(39.37, -101.49) * mm});
            skArc(sketch, "E9.31.3", {"start": v(47.72, -100.9) * mm, "mid": v(46.6, -99.84) * mm, "end": v(45.34, -98.96) * mm});
            skArc(sketch, "E9.31.4", {"start": v(39.18, -105.72) * mm, "mid": v(39.1, -107.15) * mm, "end": v(38.73, -108.53) * mm});
            skArc(sketch, "E9.31.5", {"start": v(48.51, -101.77) * mm, "mid": v(49.58, -102.72) * mm, "end": v(50.84, -103.41) * mm});
            skLineSegment(sketch, "E9.31.6", {"start": v(39.1, -104.54) * mm, "end": v(39.18, -105.72) * mm});
            skLineSegment(sketch, "E9.31.7", {"start": v(47.72, -100.9) * mm, "end": v(48.51, -101.77) * mm});
            skArc(sketch, "E9.32.0", {"start": v(56.33, -93.15) * mm, "mid": v(54.5, -92.79) * mm, "end": v(52.7, -93.3) * mm});
            skArc(sketch, "E9.32.1", {"start": v(50.68, -96.34) * mm, "mid": v(51.32, -94.58) * mm, "end": v(52.7, -93.3) * mm});
            skArc(sketch, "E9.32.2", {"start": v(50.76, -99.4) * mm, "mid": v(50.6, -97.87) * mm, "end": v(50.68, -96.34) * mm});
            skArc(sketch, "E9.32.3", {"start": v(58.91, -94.8) * mm, "mid": v(57.68, -93.88) * mm, "end": v(56.33, -93.15) * mm});
            skArc(sketch, "E9.32.4", {"start": v(50.97, -100.56) * mm, "mid": v(51.07, -102) * mm, "end": v(50.84, -103.41) * mm});
            skArc(sketch, "E9.32.5", {"start": v(59.8, -95.58) * mm, "mid": v(60.97, -96.4) * mm, "end": v(62.3, -96.94) * mm});
            skLineSegment(sketch, "E9.32.6", {"start": v(50.76, -99.4) * mm, "end": v(50.97, -100.56) * mm});
            skLineSegment(sketch, "E9.32.7", {"start": v(58.91, -94.8) * mm, "end": v(59.8, -95.58) * mm});
            skArc(sketch, "E9.33.0", {"start": v(66.58, -86.12) * mm, "mid": v(64.71, -85.97) * mm, "end": v(62.98, -86.69) * mm});
            skArc(sketch, "E9.33.1", {"start": v(61.33, -89.93) * mm, "mid": v(61.77, -88.11) * mm, "end": v(62.98, -86.69) * mm});
            skArc(sketch, "E9.33.2", {"start": v(61.76, -92.97) * mm, "mid": v(61.43, -91.47) * mm, "end": v(61.33, -89.93) * mm});
            skArc(sketch, "E9.33.3", {"start": v(69.33, -87.47) * mm, "mid": v(68, -86.69) * mm, "end": v(66.58, -86.12) * mm});
            skArc(sketch, "E9.33.4", {"start": v(62.1, -94.1) * mm, "mid": v(62.36, -95.5) * mm, "end": v(62.3, -96.94) * mm});
            skArc(sketch, "E9.33.5", {"start": v(70.3, -88.14) * mm, "mid": v(71.56, -88.82) * mm, "end": v(72.95, -89.2) * mm});
            skLineSegment(sketch, "E9.33.6", {"start": v(61.76, -92.97) * mm, "end": v(62.1, -94.1) * mm});
            skLineSegment(sketch, "E9.33.7", {"start": v(69.33, -87.47) * mm, "end": v(70.3, -88.14) * mm});
            skArc(sketch, "E9.34.0", {"start": v(75.96, -77.97) * mm, "mid": v(74.1, -78.04) * mm, "end": v(72.46, -78.95) * mm});
            skArc(sketch, "E9.34.1", {"start": v(71.18, -82.35) * mm, "mid": v(71.4, -80.5) * mm, "end": v(72.46, -78.95) * mm});
            skArc(sketch, "E9.34.2", {"start": v(71.95, -85.32) * mm, "mid": v(71.46, -83.87) * mm, "end": v(71.18, -82.35) * mm});
            skArc(sketch, "E9.34.3", {"start": v(78.85, -79) * mm, "mid": v(77.44, -78.37) * mm, "end": v(75.96, -77.97) * mm});
            skArc(sketch, "E9.34.4", {"start": v(72.42, -86.4) * mm, "mid": v(72.84, -87.78) * mm, "end": v(72.95, -89.2) * mm});
            skArc(sketch, "E9.34.5", {"start": v(79.89, -79.55) * mm, "mid": v(81.22, -80.09) * mm, "end": v(82.64, -80.31) * mm});
            skLineSegment(sketch, "E9.34.6", {"start": v(71.95, -85.32) * mm, "end": v(72.42, -86.4) * mm});
            skLineSegment(sketch, "E9.34.7", {"start": v(78.85, -79) * mm, "end": v(79.89, -79.55) * mm});
            skArc(sketch, "E9.35.0", {"start": v(84.35, -68.8) * mm, "mid": v(82.5, -69.08) * mm, "end": v(80.98, -70.17) * mm});
            skArc(sketch, "E9.35.1", {"start": v(80.1, -73.7) * mm, "mid": v(80.12, -71.83) * mm, "end": v(80.98, -70.17) * mm});
            skArc(sketch, "E9.35.2", {"start": v(81.21, -76.56) * mm, "mid": v(80.55, -75.17) * mm, "end": v(80.1, -73.7) * mm});
            skArc(sketch, "E9.35.3", {"start": v(87.34, -69.49) * mm, "mid": v(85.87, -69.03) * mm, "end": v(84.35, -68.8) * mm});
            skArc(sketch, "E9.35.4", {"start": v(81.8, -77.59) * mm, "mid": v(82.37, -78.9) * mm, "end": v(82.64, -80.31) * mm});
            skArc(sketch, "E9.35.5", {"start": v(88.44, -69.93) * mm, "mid": v(89.82, -70.3) * mm, "end": v(91.26, -70.37) * mm});
            skLineSegment(sketch, "E9.35.6", {"start": v(81.21, -76.56) * mm, "end": v(81.8, -77.59) * mm});
            skLineSegment(sketch, "E9.35.7", {"start": v(87.34, -69.49) * mm, "end": v(88.44, -69.93) * mm});
            skArc(sketch, "E9.36.0", {"start": v(91.65, -58.74) * mm, "mid": v(89.84, -59.23) * mm, "end": v(88.45, -60.48) * mm});
            skArc(sketch, "E9.36.1", {"start": v(87.98, -64.1) * mm, "mid": v(87.79, -62.23) * mm, "end": v(88.45, -60.48) * mm});
            skArc(sketch, "E9.36.2", {"start": v(89.4, -66.8) * mm, "mid": v(88.6, -65.5) * mm, "end": v(87.98, -64.1) * mm});
            skArc(sketch, "E9.36.3", {"start": v(94.7, -59.08) * mm, "mid": v(93.18, -58.8) * mm, "end": v(91.65, -58.74) * mm});
            skArc(sketch, "E9.36.4", {"start": v(90.11, -67.76) * mm, "mid": v(90.83, -69) * mm, "end": v(91.26, -70.37) * mm});
            skArc(sketch, "E9.36.5", {"start": v(95.83, -59.39) * mm, "mid": v(97.25, -59.6) * mm, "end": v(98.68, -59.5) * mm});
            skLineSegment(sketch, "E9.36.6", {"start": v(89.4, -66.8) * mm, "end": v(90.11, -67.76) * mm});
            skLineSegment(sketch, "E9.36.7", {"start": v(94.7, -59.08) * mm, "end": v(95.83, -59.39) * mm});
            skArc(sketch, "E9.37.0", {"start": v(97.74, -47.9) * mm, "mid": v(96, -48.6) * mm, "end": v(94.77, -50) * mm});
            skArc(sketch, "E9.37.1", {"start": v(94.72, -53.65) * mm, "mid": v(94.3, -51.82) * mm, "end": v(94.77, -50) * mm});
            skArc(sketch, "E9.37.2", {"start": v(96.44, -56.18) * mm, "mid": v(95.49, -54.98) * mm, "end": v(94.72, -53.65) * mm});
            skArc(sketch, "E9.37.3", {"start": v(100.81, -47.9) * mm, "mid": v(99.28, -47.79) * mm, "end": v(97.74, -47.9) * mm});
            skArc(sketch, "E9.37.4", {"start": v(97.25, -57.04) * mm, "mid": v(98.1, -58.2) * mm, "end": v(98.68, -59.5) * mm});
            skArc(sketch, "E9.37.5", {"start": v(101.98, -48.08) * mm, "mid": v(103.41, -48.14) * mm, "end": v(104.82, -47.87) * mm});
            skLineSegment(sketch, "E9.37.6", {"start": v(96.44, -56.18) * mm, "end": v(97.25, -57.04) * mm});
            skLineSegment(sketch, "E9.37.7", {"start": v(100.81, -47.9) * mm, "end": v(101.98, -48.08) * mm});
            skArc(sketch, "E9.38.0", {"start": v(102.57, -36.45) * mm, "mid": v(100.92, -37.34) * mm, "end": v(99.85, -38.88) * mm});
            skArc(sketch, "E9.38.1", {"start": v(100.21, -42.5) * mm, "mid": v(99.6, -40.73) * mm, "end": v(99.85, -38.88) * mm});
            skArc(sketch, "E9.38.2", {"start": v(102.22, -44.82) * mm, "mid": v(101.13, -43.73) * mm, "end": v(100.21, -42.5) * mm});
            skArc(sketch, "E9.38.3", {"start": v(105.61, -36.1) * mm, "mid": v(104.08, -36.16) * mm, "end": v(102.57, -36.45) * mm});
            skArc(sketch, "E9.38.4", {"start": v(103.12, -45.58) * mm, "mid": v(104.1, -46.63) * mm, "end": v(104.82, -47.87) * mm});
            skArc(sketch, "E9.38.5", {"start": v(106.8, -36.14) * mm, "mid": v(108.22, -36.03) * mm, "end": v(109.6, -35.6) * mm});
            skLineSegment(sketch, "E9.38.6", {"start": v(102.22, -44.82) * mm, "end": v(103.12, -45.58) * mm});
            skLineSegment(sketch, "E9.38.7", {"start": v(105.61, -36.1) * mm, "end": v(106.8, -36.14) * mm});
            skArc(sketch, "E9.39.0", {"start": v(106.05, -24.52) * mm, "mid": v(104.52, -25.6) * mm, "end": v(103.63, -27.24) * mm});
            skArc(sketch, "E9.39.1", {"start": v(104.4, -30.8) * mm, "mid": v(103.6, -29.11) * mm, "end": v(103.63, -27.24) * mm});
            skArc(sketch, "E9.39.2", {"start": v(106.66, -32.88) * mm, "mid": v(105.46, -31.92) * mm, "end": v(104.4, -30.8) * mm});
            skArc(sketch, "E9.39.3", {"start": v(109.04, -23.82) * mm, "mid": v(107.52, -24.06) * mm, "end": v(106.05, -24.52) * mm});
            skArc(sketch, "E9.39.4", {"start": v(107.64, -33.53) * mm, "mid": v(108.74, -34.46) * mm, "end": v(109.6, -35.6) * mm});
            skArc(sketch, "E9.39.5", {"start": v(110.22, -23.73) * mm, "mid": v(111.63, -23.46) * mm, "end": v(112.94, -22.88) * mm});
            skLineSegment(sketch, "E9.39.6", {"start": v(106.66, -32.88) * mm, "end": v(107.64, -33.53) * mm});
            skLineSegment(sketch, "E9.39.7", {"start": v(109.04, -23.82) * mm, "end": v(110.22, -23.73) * mm});
            skArc(sketch, "E9.40.0", {"start": v(108.16, -12.27) * mm, "mid": v(106.75, -13.51) * mm, "end": v(106.06, -15.25) * mm});
            skArc(sketch, "E9.40.1", {"start": v(107.24, -18.7) * mm, "mid": v(106.24, -17.11) * mm, "end": v(106.06, -15.25) * mm});
            skArc(sketch, "E9.40.2", {"start": v(109.71, -20.5) * mm, "mid": v(108.4, -19.7) * mm, "end": v(107.24, -18.7) * mm});
            skArc(sketch, "E9.40.3", {"start": v(111.05, -11.24) * mm, "mid": v(109.56, -11.65) * mm, "end": v(108.16, -12.27) * mm});
            skArc(sketch, "E9.40.4", {"start": v(110.76, -21.04) * mm, "mid": v(111.95, -21.84) * mm, "end": v(112.94, -22.88) * mm});
            skArc(sketch, "E9.40.5", {"start": v(112.2, -11.01) * mm, "mid": v(113.57, -10.58) * mm, "end": v(114.81, -9.86) * mm});
            skLineSegment(sketch, "E9.40.6", {"start": v(109.71, -20.5) * mm, "end": v(110.76, -21.04) * mm});
            skLineSegment(sketch, "E9.40.7", {"start": v(111.05, -11.24) * mm, "end": v(112.2, -11.01) * mm});
            skArc(sketch, "E9.41.0", {"start": v(108.85, 0.14) * mm, "mid": v(107.6, -1.25) * mm, "end": v(107.11, -3.06) * mm});
            skArc(sketch, "E9.41.1", {"start": v(108.67, -6.35) * mm, "mid": v(107.5, -4.9) * mm, "end": v(107.11, -3.06) * mm});
            skArc(sketch, "E9.41.2", {"start": v(111.33, -7.86) * mm, "mid": v(109.94, -7.2) * mm, "end": v(108.67, -6.35) * mm});
            skArc(sketch, "E9.41.3", {"start": v(111.6, 1.5) * mm, "mid": v(110.18, 0.92) * mm, "end": v(108.85, 0.14) * mm});
            skArc(sketch, "E9.41.4", {"start": v(112.44, -8.28) * mm, "mid": v(113.71, -8.94) * mm, "end": v(114.81, -9.86) * mm});
            skArc(sketch, "E9.41.5", {"start": v(112.73, 1.85) * mm, "mid": v(114.04, 2.43) * mm, "end": v(115.19, 3.3) * mm});
            skLineSegment(sketch, "E9.41.6", {"start": v(111.33, -7.86) * mm, "end": v(112.44, -8.28) * mm});
            skLineSegment(sketch, "E9.41.7", {"start": v(111.6, 1.5) * mm, "end": v(112.73, 1.85) * mm});
            skArc(sketch, "E9.42.0", {"start": v(108.13, 12.54) * mm, "mid": v(107.04, 11.02) * mm, "end": v(106.76, 9.17) * mm});
            skArc(sketch, "E9.42.1", {"start": v(108.68, 6.08) * mm, "mid": v(107.35, 7.4) * mm, "end": v(106.76, 9.17) * mm});
            skArc(sketch, "E9.42.2", {"start": v(111.5, 4.88) * mm, "mid": v(110.05, 5.37) * mm, "end": v(108.68, 6.08) * mm});
            skArc(sketch, "E9.42.3", {"start": v(110.7, 14.2) * mm, "mid": v(109.35, 13.47) * mm, "end": v(108.13, 12.54) * mm});
            skArc(sketch, "E9.42.4", {"start": v(112.65, 4.59) * mm, "mid": v(114, 4.08) * mm, "end": v(115.19, 3.3) * mm});
            skArc(sketch, "E9.42.5", {"start": v(111.78, 14.69) * mm, "mid": v(113.02, 15.41) * mm, "end": v(114.06, 16.4) * mm});
            skLineSegment(sketch, "E9.42.6", {"start": v(111.5, 4.88) * mm, "end": v(112.65, 4.59) * mm});
            skLineSegment(sketch, "E9.42.7", {"start": v(110.7, 14.2) * mm, "end": v(111.78, 14.69) * mm});
            skArc(sketch, "E9.43.0", {"start": v(106, 24.79) * mm, "mid": v(105.09, 23.15) * mm, "end": v(105.02, 21.28) * mm});
            skArc(sketch, "E9.43.1", {"start": v(107.28, 18.43) * mm, "mid": v(105.8, 19.58) * mm, "end": v(105.02, 21.28) * mm});
            skArc(sketch, "E9.43.2", {"start": v(110.22, 17.56) * mm, "mid": v(108.72, 17.88) * mm, "end": v(107.28, 18.43) * mm});
            skArc(sketch, "E9.43.3", {"start": v(108.36, 26.73) * mm, "mid": v(107.1, 25.85) * mm, "end": v(106, 24.79) * mm});
            skArc(sketch, "E9.43.4", {"start": v(111.4, 17.4) * mm, "mid": v(112.78, 17.05) * mm, "end": v(114.06, 16.4) * mm});
            skArc(sketch, "E9.43.5", {"start": v(109.38, 27.33) * mm, "mid": v(110.53, 28.2) * mm, "end": v(111.45, 29.3) * mm});
            skLineSegment(sketch, "E9.43.6", {"start": v(110.22, 17.56) * mm, "end": v(111.4, 17.4) * mm});
            skLineSegment(sketch, "E9.43.7", {"start": v(108.36, 26.73) * mm, "end": v(109.38, 27.33) * mm});
            skArc(sketch, "E9.44.0", {"start": v(102.48, 36.7) * mm, "mid": v(101.76, 34.98) * mm, "end": v(101.91, 33.11) * mm});
            skArc(sketch, "E9.44.1", {"start": v(104.48, 30.54) * mm, "mid": v(102.89, 31.52) * mm, "end": v(101.91, 33.11) * mm});
            skArc(sketch, "E9.44.2", {"start": v(107.5, 30) * mm, "mid": v(105.97, 30.16) * mm, "end": v(104.48, 30.54) * mm});
            skArc(sketch, "E9.44.3", {"start": v(104.6, 38.91) * mm, "mid": v(103.46, 37.89) * mm, "end": v(102.48, 36.7) * mm});
            skArc(sketch, "E9.44.4", {"start": v(108.68, 29.98) * mm, "mid": v(110.1, 29.8) * mm, "end": v(111.45, 29.3) * mm});
            skArc(sketch, "E9.44.5", {"start": v(105.55, 39.62) * mm, "mid": v(106.6, 40.61) * mm, "end": v(107.38, 41.8) * mm});
            skLineSegment(sketch, "E9.44.6", {"start": v(107.5, 30) * mm, "end": v(108.68, 29.98) * mm});
            skLineSegment(sketch, "E9.44.7", {"start": v(104.6, 38.91) * mm, "end": v(105.55, 39.62) * mm});
            skArc(sketch, "E9.45.0", {"start": v(97.62, 48.15) * mm, "mid": v(97.11, 46.35) * mm, "end": v(97.47, 44.51) * mm});
            skArc(sketch, "E9.45.1", {"start": v(100.32, 42.25) * mm, "mid": v(98.62, 43.04) * mm, "end": v(97.47, 44.51) * mm});
            skArc(sketch, "E9.45.2", {"start": v(103.38, 42.07) * mm, "mid": v(101.84, 42.04) * mm, "end": v(100.32, 42.25) * mm});
            skArc(sketch, "E9.45.3", {"start": v(99.5, 50.58) * mm, "mid": v(98.47, 49.44) * mm, "end": v(97.62, 48.15) * mm});
            skArc(sketch, "E9.45.4", {"start": v(104.56, 42.18) * mm, "mid": v(106, 42.15) * mm, "end": v(107.38, 41.8) * mm});
            skArc(sketch, "E9.45.5", {"start": v(100.35, 51.4) * mm, "mid": v(101.27, 52.5) * mm, "end": v(101.92, 53.78) * mm});
            skLineSegment(sketch, "E9.45.6", {"start": v(103.38, 42.07) * mm, "end": v(104.56, 42.18) * mm});
            skLineSegment(sketch, "E9.45.7", {"start": v(99.5, 50.58) * mm, "end": v(100.35, 51.4) * mm});
            skArc(sketch, "E9.46.0", {"start": v(91.5, 58.96) * mm, "mid": v(91.2, 57.12) * mm, "end": v(91.76, 55.33) * mm});
            skArc(sketch, "E9.46.1", {"start": v(94.85, 53.4) * mm, "mid": v(93.08, 54) * mm, "end": v(91.76, 55.33) * mm});
            skArc(sketch, "E9.46.2", {"start": v(97.91, 53.58) * mm, "mid": v(96.39, 53.38) * mm, "end": v(94.85, 53.4) * mm});
            skArc(sketch, "E9.46.3", {"start": v(93.08, 61.6) * mm, "mid": v(92.2, 60.34) * mm, "end": v(91.5, 58.96) * mm});
            skArc(sketch, "E9.46.4", {"start": v(99.07, 53.82) * mm, "mid": v(100.5, 53.96) * mm, "end": v(101.92, 53.78) * mm});
            skArc(sketch, "E9.46.5", {"start": v(93.83, 62.5) * mm, "mid": v(94.62, 63.7) * mm, "end": v(95.12, 65.04) * mm});
            skLineSegment(sketch, "E9.46.6", {"start": v(97.91, 53.58) * mm, "end": v(99.07, 53.82) * mm});
            skLineSegment(sketch, "E9.46.7", {"start": v(93.08, 61.6) * mm, "end": v(93.83, 62.5) * mm});
            skArc(sketch, "E9.47.0", {"start": v(84.18, 69.01) * mm, "mid": v(84.09, 67.14) * mm, "end": v(84.86, 65.43) * mm});
            skArc(sketch, "E9.47.1", {"start": v(88.14, 63.87) * mm, "mid": v(86.31, 64.26) * mm, "end": v(84.86, 65.43) * mm});
            skArc(sketch, "E9.47.2", {"start": v(91.17, 64.39) * mm, "mid": v(89.67, 64.02) * mm, "end": v(88.14, 63.87) * mm});
            skArc(sketch, "E9.47.3", {"start": v(85.45, 71.8) * mm, "mid": v(84.71, 70.45) * mm, "end": v(84.18, 69.01) * mm});
            skArc(sketch, "E9.47.4", {"start": v(92.29, 64.76) * mm, "mid": v(93.69, 65.06) * mm, "end": v(95.12, 65.04) * mm});
            skArc(sketch, "E9.47.5", {"start": v(86.1, 72.79) * mm, "mid": v(86.74, 74.07) * mm, "end": v(87.09, 75.46) * mm});
            skLineSegment(sketch, "E9.47.6", {"start": v(91.17, 64.39) * mm, "end": v(92.29, 64.76) * mm});
            skLineSegment(sketch, "E9.47.7", {"start": v(85.45, 71.8) * mm, "end": v(86.1, 72.79) * mm});
            skArc(sketch, "E9.48.0", {"start": v(75.77, 78.16) * mm, "mid": v(75.89, 76.29) * mm, "end": v(76.84, 74.68) * mm});
            skArc(sketch, "E9.48.1", {"start": v(80.29, 73.5) * mm, "mid": v(78.43, 73.68) * mm, "end": v(76.84, 74.68) * mm});
            skArc(sketch, "E9.48.2", {"start": v(83.23, 74.36) * mm, "mid": v(81.8, 73.82) * mm, "end": v(80.29, 73.5) * mm});
            skArc(sketch, "E9.48.3", {"start": v(76.7, 81.08) * mm, "mid": v(76.13, 79.65) * mm, "end": v(75.77, 78.16) * mm});
            skArc(sketch, "E9.48.4", {"start": v(84.3, 74.86) * mm, "mid": v(85.66, 75.32) * mm, "end": v(87.09, 75.46) * mm});
            skArc(sketch, "E9.48.5", {"start": v(77.24, 82.13) * mm, "mid": v(77.74, 83.48) * mm, "end": v(77.92, 84.9) * mm});
            skLineSegment(sketch, "E9.48.6", {"start": v(83.23, 74.36) * mm, "end": v(84.3, 74.86) * mm});
            skLineSegment(sketch, "E9.48.7", {"start": v(76.7, 81.08) * mm, "end": v(77.24, 82.13) * mm});
            skArc(sketch, "E9.49.0", {"start": v(66.36, 86.28) * mm, "mid": v(66.7, 84.44) * mm, "end": v(67.83, 82.95) * mm});
            skArc(sketch, "E9.49.1", {"start": v(71.39, 82.18) * mm, "mid": v(69.52, 82.14) * mm, "end": v(67.83, 82.95) * mm});
            skArc(sketch, "E9.49.2", {"start": v(74.21, 83.36) * mm, "mid": v(72.84, 82.67) * mm, "end": v(71.39, 82.18) * mm});
            skArc(sketch, "E9.49.3", {"start": v(66.97, 89.3) * mm, "mid": v(66.55, 87.8) * mm, "end": v(66.36, 86.28) * mm});
            skArc(sketch, "E9.49.4", {"start": v(75.22, 83.98) * mm, "mid": v(76.52, 84.6) * mm, "end": v(77.92, 84.9) * mm});
            skArc(sketch, "E9.49.5", {"start": v(67.37, 90.4) * mm, "mid": v(67.71, 91.8) * mm, "end": v(67.73, 93.23) * mm});
            skLineSegment(sketch, "E9.49.6", {"start": v(74.21, 83.36) * mm, "end": v(75.22, 83.98) * mm});
            skLineSegment(sketch, "E9.49.7", {"start": v(66.97, 89.3) * mm, "end": v(67.37, 90.4) * mm});
            skArc(sketch, "E9.50.0", {"start": v(56.1, 93.29) * mm, "mid": v(56.64, 91.5) * mm, "end": v(57.93, 90.14) * mm});
            skArc(sketch, "E9.50.1", {"start": v(61.55, 89.78) * mm, "mid": v(59.7, 89.53) * mm, "end": v(57.93, 90.14) * mm});
            skArc(sketch, "E9.50.2", {"start": v(64.23, 91.28) * mm, "mid": v(62.95, 90.43) * mm, "end": v(61.55, 89.78) * mm});
            skArc(sketch, "E9.50.3", {"start": v(56.35, 96.34) * mm, "mid": v(56.1, 94.82) * mm, "end": v(56.1, 93.29) * mm});
            skArc(sketch, "E9.50.4", {"start": v(65.15, 92) * mm, "mid": v(66.38, 92.76) * mm, "end": v(67.73, 93.23) * mm});
            skArc(sketch, "E9.50.5", {"start": v(56.63, 97.49) * mm, "mid": v(56.8, 98.91) * mm, "end": v(56.67, 100.34) * mm});
            skLineSegment(sketch, "E9.50.6", {"start": v(64.23, 91.28) * mm, "end": v(65.15, 92) * mm});
            skLineSegment(sketch, "E9.50.7", {"start": v(56.35, 96.34) * mm, "end": v(56.63, 97.49) * mm});
            skArc(sketch, "E9.51.0", {"start": v(45.1, 99.07) * mm, "mid": v(45.84, 97.35) * mm, "end": v(47.28, 96.16) * mm});
            skArc(sketch, "E9.51.1", {"start": v(50.92, 96.2) * mm, "mid": v(49.1, 95.75) * mm, "end": v(47.28, 96.16) * mm});
            skArc(sketch, "E9.51.2", {"start": v(53.4, 98) * mm, "mid": v(52.23, 97.02) * mm, "end": v(50.92, 96.2) * mm});
            skArc(sketch, "E9.51.3", {"start": v(45, 102.14) * mm, "mid": v(44.93, 100.6) * mm, "end": v(45.1, 99.07) * mm});
            skArc(sketch, "E9.51.4", {"start": v(54.24, 98.84) * mm, "mid": v(55.37, 99.73) * mm, "end": v(56.67, 100.34) * mm});
            skArc(sketch, "E9.51.5", {"start": v(45.15, 103.3) * mm, "mid": v(45.16, 104.74) * mm, "end": v(44.86, 106.15) * mm});
            skLineSegment(sketch, "E9.51.6", {"start": v(53.4, 98) * mm, "end": v(54.24, 98.84) * mm});
            skLineSegment(sketch, "E9.51.7", {"start": v(45, 102.14) * mm, "end": v(45.15, 103.3) * mm});
            skArc(sketch, "E9.52.0", {"start": v(33.5, 103.57) * mm, "mid": v(34.44, 101.95) * mm, "end": v(36, 100.92) * mm});
            skArc(sketch, "E9.52.1", {"start": v(39.62, 101.39) * mm, "mid": v(37.87, 100.72) * mm, "end": v(36, 100.92) * mm});
            skArc(sketch, "E9.52.2", {"start": v(41.88, 103.46) * mm, "mid": v(40.83, 102.34) * mm, "end": v(39.62, 101.39) * mm});
            skArc(sketch, "E9.52.3", {"start": v(33.07, 106.6) * mm, "mid": v(33.17, 105.07) * mm, "end": v(33.5, 103.57) * mm});
            skArc(sketch, "E9.52.4", {"start": v(42.62, 104.38) * mm, "mid": v(43.64, 105.39) * mm, "end": v(44.86, 106.15) * mm});
            skArc(sketch, "E9.52.5", {"start": v(33.08, 107.78) * mm, "mid": v(32.93, 109.2) * mm, "end": v(32.47, 110.57) * mm});
            skLineSegment(sketch, "E9.52.6", {"start": v(41.88, 103.46) * mm, "end": v(42.62, 104.38) * mm});
            skLineSegment(sketch, "E9.52.7", {"start": v(33.07, 106.6) * mm, "end": v(33.08, 107.78) * mm});
            skArc(sketch, "E9.53.0", {"start": v(21.48, 106.71) * mm, "mid": v(22.6, 105.2) * mm, "end": v(24.27, 104.37) * mm});
            skArc(sketch, "E9.53.1", {"start": v(27.8, 105.24) * mm, "mid": v(26.14, 104.38) * mm, "end": v(24.27, 104.37) * mm});
            skArc(sketch, "E9.53.2", {"start": v(29.82, 107.56) * mm, "mid": v(28.9, 106.32) * mm, "end": v(27.8, 105.24) * mm});
            skArc(sketch, "E9.53.3", {"start": v(20.7, 109.68) * mm, "mid": v(20.98, 108.16) * mm, "end": v(21.48, 106.71) * mm});
            skArc(sketch, "E9.53.4", {"start": v(30.45, 108.55) * mm, "mid": v(31.34, 109.68) * mm, "end": v(32.47, 110.57) * mm});
            skArc(sketch, "E9.53.5", {"start": v(20.57, 110.85) * mm, "mid": v(20.26, 112.25) * mm, "end": v(19.65, 113.55) * mm});
            skLineSegment(sketch, "E9.53.6", {"start": v(29.82, 107.56) * mm, "end": v(30.45, 108.55) * mm});
            skLineSegment(sketch, "E9.53.7", {"start": v(20.7, 109.68) * mm, "end": v(20.57, 110.85) * mm});
            skArc(sketch, "E9.54.0", {"start": v(9.18, 108.47) * mm, "mid": v(10.46, 107.1) * mm, "end": v(12.21, 106.46) * mm});
            skArc(sketch, "E9.54.1", {"start": v(15.63, 107.73) * mm, "mid": v(14.07, 106.68) * mm, "end": v(12.21, 106.46) * mm});
            skArc(sketch, "E9.54.2", {"start": v(17.36, 110.25) * mm, "mid": v(16.59, 108.93) * mm, "end": v(15.63, 107.73) * mm});
            skArc(sketch, "E9.54.3", {"start": v(8.06, 111.32) * mm, "mid": v(8.51, 109.85) * mm, "end": v(9.18, 108.47) * mm});
            skArc(sketch, "E9.54.4", {"start": v(17.87, 111.32) * mm, "mid": v(18.64, 112.53) * mm, "end": v(19.65, 113.55) * mm});
            skArc(sketch, "E9.54.5", {"start": v(7.8, 112.47) * mm, "mid": v(7.34, 113.83) * mm, "end": v(6.58, 115.05) * mm});
            skLineSegment(sketch, "E9.54.6", {"start": v(17.36, 110.25) * mm, "end": v(17.87, 111.32) * mm});
            skLineSegment(sketch, "E9.54.7", {"start": v(8.06, 111.32) * mm, "end": v(7.8, 112.47) * mm});
            skCircle(sketch, "E10", {"center": v(0, 0) * mm, "radius": 104.65 * mm});
            skCircle(sketch, "E11", {"center": v(0, 0) * mm, "radius": 113.62 * mm});
            skCircle(sketch, "E12", {"center": v(0, 0) * mm, "radius": 65 * mm});
            skCircle(sketch, "E13", {"center": v(0, 72) * mm, "radius": 5.25 * mm});
            skCircle(sketch, "E14.1.0", {"center": v(-68.48, 22.25) * mm, "radius": 5.25 * mm});
            skCircle(sketch, "E14.2.0", {"center": v(-42.32, -58.25) * mm, "radius": 5.25 * mm});
            skCircle(sketch, "E14.3.0", {"center": v(42.32, -58.25) * mm, "radius": 5.25 * mm});
            skCircle(sketch, "E14.4.0", {"center": v(68.48, 22.25) * mm, "radius": 5.25 * mm});
            skSolve(sketch);
        }
        {
            var Q0;
            Q0=makeQuery(id+"F0.imprint","IMPRINT",FACE,{"disambiguationData":[TD([[makeQuery(id+"F0.imprint","IMPRINT",EDGE,{"derivedFrom":sQuery(id+"F0.wireOp",EDGE,"E1")}),-1.0]])]});
            extrude(context, id + "F1", {"entities" : qUnion([Q0]), "endBound" : BoundingType.SYMMETRIC, "depth" : 3.16 * mm});
        }
        {
            var Q0;
            Q0=makeQuery(id+"F0.imprint","IMPRINT",FACE,{"disambiguationData":[TD([[makeQuery(id+"F0.imprint","IMPRINT",EDGE,{"derivedFrom":sQuery(id+"F0.wireOp",EDGE,"E10")}),1.0]])]});
            extrude(context, id + "F2", {"entities" : qUnion([Q0]), "operationType" : NewBodyOperationType.ADD, "endBound" : BoundingType.SYMMETRIC, "depth" : 4.5 * mm});
        }
        {
            var Q0;
            Q0=makeQuery(id+"F2.opExtrude","CAP_FACE",FACE,{"disambiguationData":[OSD([sQuery(id+"F0.wireOp",EDGE,"E10"),sQuery(id+"F0.wireOp",EDGE,"E12"),sQuery(id+"F0.wireOp",EDGE,"E13"),sQuery(id+"F0.wireOp",EDGE,"E14.1.0"),sQuery(id+"F0.wireOp",EDGE,"E14.2.0"),sQuery(id+"F0.wireOp",EDGE,"E14.3.0"),sQuery(id+"F0.wireOp",EDGE,"E14.4.0")])],"isStart":false});
            var sketch = newSketch(context, id + "F3", { "sketchPlane" : qUnion([Q0])});
            skArc(sketch, "E15", {"start": v(69.48, -71.33) * mm, "mid": v(74.29, -66.3) * mm, "end": v(78.73, -60.96) * mm});
            skArc(sketch, "E16", {"start": v(48.9, -50.2) * mm, "mid": v(52.28, -46.66) * mm, "end": v(55.41, -42.9) * mm});
            skLineSegment(sketch, "E17", {"start": v(69.07, 11.87) * mm, "end": v(98.14, 16.86) * mm});
            skLineSegment(sketch, "E18", {"start": v(48.9, -50.2) * mm, "end": v(69.48, -71.33) * mm});
            skLineSegment(sketch, "E19", {"start": v(70.05, 2.14) * mm, "end": v(99.53, 3.04) * mm});
            skLineSegment(sketch, "E20", {"start": v(70.08, 0.3) * mm, "end": v(99.57, 0.44) * mm});
            skLineSegment(sketch, "E21", {"start": v(69.44, -9.45) * mm, "end": v(98.67, -13.43) * mm});
            skLineSegment(sketch, "E22", {"start": v(69.17, -11.26) * mm, "end": v(98.28, -16) * mm});
            skLineSegment(sketch, "E23", {"start": v(66.93, -20.78) * mm, "end": v(95.1, -29.53) * mm});
            skLineSegment(sketch, "E24", {"start": v(66.36, -22.53) * mm, "end": v(94.3, -32) * mm});
            skLineSegment(sketch, "E25", {"start": v(62.58, -31.54) * mm, "end": v(88.92, -44.82) * mm});
            skLineSegment(sketch, "E26", {"start": v(61.73, -33.17) * mm, "end": v(87.72, -47.13) * mm});
            skLineSegment(sketch, "E27", {"start": v(56.52, -41.44) * mm, "end": v(80.3, -58.88) * mm});
            skLineSegment(sketch, "E28", {"start": v(55.41, -42.9) * mm, "end": v(78.73, -60.96) * mm});
            skArc(sketch, "E29.trimOffspring", {"start": v(80.3, -58.88) * mm, "mid": v(84.21, -53.13) * mm, "end": v(87.72, -47.13) * mm});
            skArc(sketch, "E30.trimOffspring", {"start": v(88.92, -44.82) * mm, "mid": v(91.83, -38.5) * mm, "end": v(94.3, -32) * mm});
            skArc(sketch, "E31.trimOffspring", {"start": v(99.53, 3.04) * mm, "mid": v(99.07, 9.98) * mm, "end": v(98.14, 16.86) * mm});
            skArc(sketch, "E32.trimOffspring", {"start": v(70.05, 2.14) * mm, "mid": v(69.73, 7.02) * mm, "end": v(69.07, 11.87) * mm});
            skArc(sketch, "E33.trimOffspring", {"start": v(98.67, -13.43) * mm, "mid": v(99.36, -6.51) * mm, "end": v(99.57, 0.44) * mm});
            skArc(sketch, "E34.trimOffspring", {"start": v(95.1, -29.53) * mm, "mid": v(96.92, -22.82) * mm, "end": v(98.28, -16) * mm});
            skArc(sketch, "E35.trimOffspring", {"start": v(66.93, -20.78) * mm, "mid": v(68.21, -16.06) * mm, "end": v(69.17, -11.26) * mm});
            skArc(sketch, "E36.trimOffspring", {"start": v(69.44, -9.45) * mm, "mid": v(69.93, -4.58) * mm, "end": v(70.08, 0.3) * mm});
            skArc(sketch, "E37.trimOffspring", {"start": v(62.58, -31.54) * mm, "mid": v(64.63, -27.1) * mm, "end": v(66.36, -22.53) * mm});
            skArc(sketch, "E38.trimOffspring", {"start": v(56.52, -41.44) * mm, "mid": v(59.27, -37.4) * mm, "end": v(61.73, -33.17) * mm});
            skLineSegment(sketch, "E39.1.0", {"start": v(40.45, 57.23) * mm, "end": v(57.47, 81.32) * mm});
            skLineSegment(sketch, "E39.1.1", {"start": v(49.34, 49.77) * mm, "end": v(70.1, 70.72) * mm});
            skLineSegment(sketch, "E39.1.2", {"start": v(50.62, 48.46) * mm, "end": v(71.93, 68.86) * mm});
            skLineSegment(sketch, "E39.1.3", {"start": v(32.09, 62.3) * mm, "end": v(45.6, 88.52) * mm});
            skLineSegment(sketch, "E39.1.4", {"start": v(41.93, 56.15) * mm, "end": v(59.58, 79.79) * mm});
            skLineSegment(sketch, "E39.1.5", {"start": v(30.44, 63.12) * mm, "end": v(43.26, 89.69) * mm});
            skLineSegment(sketch, "E39.1.6", {"start": v(21.36, 66.74) * mm, "end": v(30.35, 94.84) * mm});
            skArc(sketch, "E39.1.7", {"start": v(19.6, 67.28) * mm, "mid": v(14.87, 68.48) * mm, "end": v(10.05, 69.35) * mm});
            skLineSegment(sketch, "E39.1.8", {"start": v(56.87, 40.95) * mm, "end": v(80.81, 58.18) * mm});
            skArc(sketch, "E39.1.9", {"start": v(57.47, 81.32) * mm, "mid": v(51.65, 85.13) * mm, "end": v(45.6, 88.52) * mm});
            skLineSegment(sketch, "E39.1.10", {"start": v(19.6, 67.28) * mm, "end": v(27.86, 95.6) * mm});
            skArc(sketch, "E39.1.11", {"start": v(27.86, 95.6) * mm, "mid": v(21.13, 97.3) * mm, "end": v(14.29, 98.54) * mm});
            skLineSegment(sketch, "E39.1.12", {"start": v(62.85, 31) * mm, "end": v(89.3, 44.04) * mm});
            skArc(sketch, "E39.1.13", {"start": v(43.26, 89.69) * mm, "mid": v(36.9, 92.49) * mm, "end": v(30.35, 94.84) * mm});
            skLineSegment(sketch, "E39.1.14", {"start": v(10.05, 69.35) * mm, "end": v(14.29, 98.54) * mm});
            skArc(sketch, "E39.1.15", {"start": v(89.3, 44.04) * mm, "mid": v(86.02, 50.16) * mm, "end": v(82.3, 56.04) * mm});
            skArc(sketch, "E39.1.16", {"start": v(70.1, 70.72) * mm, "mid": v(65, 75.44) * mm, "end": v(59.58, 79.79) * mm});
            skArc(sketch, "E39.1.17", {"start": v(80.81, 58.18) * mm, "mid": v(76.56, 63.67) * mm, "end": v(71.93, 68.86) * mm});
            skLineSegment(sketch, "E39.1.18", {"start": v(57.93, 39.44) * mm, "end": v(82.3, 56.04) * mm});
            skArc(sketch, "E39.1.19", {"start": v(40.45, 57.23) * mm, "mid": v(36.35, 59.91) * mm, "end": v(32.09, 62.3) * mm});
            skArc(sketch, "E39.1.20", {"start": v(49.34, 49.77) * mm, "mid": v(45.74, 53.1) * mm, "end": v(41.93, 56.15) * mm});
            skArc(sketch, "E39.1.21", {"start": v(62.85, 31) * mm, "mid": v(60.54, 35.3) * mm, "end": v(57.93, 39.44) * mm});
            skArc(sketch, "E39.1.22", {"start": v(30.44, 63.12) * mm, "mid": v(25.97, 65.1) * mm, "end": v(21.36, 66.74) * mm});
            skArc(sketch, "E39.1.23", {"start": v(56.87, 40.95) * mm, "mid": v(53.88, 44.81) * mm, "end": v(50.62, 48.46) * mm});
            skLineSegment(sketch, "E39.2.0", {"start": v(-41.93, 56.15) * mm, "end": v(-59.58, 79.78) * mm});
            skLineSegment(sketch, "E39.2.1", {"start": v(-32.09, 62.3) * mm, "end": v(-45.6, 88.52) * mm});
            skLineSegment(sketch, "E39.2.2", {"start": v(-30.45, 63.12) * mm, "end": v(-43.26, 89.69) * mm});
            skLineSegment(sketch, "E39.2.3", {"start": v(-49.34, 49.77) * mm, "end": v(-70.1, 70.71) * mm});
            skLineSegment(sketch, "E39.2.4", {"start": v(-40.45, 57.23) * mm, "end": v(-57.47, 81.32) * mm});
            skLineSegment(sketch, "E39.2.5", {"start": v(-50.62, 48.46) * mm, "end": v(-71.93, 68.86) * mm});
            skLineSegment(sketch, "E39.2.6", {"start": v(-56.88, 40.94) * mm, "end": v(-80.81, 58.17) * mm});
            skArc(sketch, "E39.2.7", {"start": v(-57.93, 39.44) * mm, "mid": v(-60.54, 35.3) * mm, "end": v(-62.85, 31) * mm});
            skLineSegment(sketch, "E39.2.8", {"start": v(-21.37, 66.74) * mm, "end": v(-30.36, 94.83) * mm});
            skArc(sketch, "E39.2.9", {"start": v(-59.58, 79.78) * mm, "mid": v(-65, 75.43) * mm, "end": v(-70.1, 70.71) * mm});
            skLineSegment(sketch, "E39.2.10", {"start": v(-57.93, 39.44) * mm, "end": v(-82.3, 56.04) * mm});
            skArc(sketch, "E39.2.11", {"start": v(-82.3, 56.04) * mm, "mid": v(-86.02, 50.16) * mm, "end": v(-89.3, 44.04) * mm});
            skLineSegment(sketch, "E39.2.12", {"start": v(-10.05, 69.35) * mm, "end": v(-14.29, 98.54) * mm});
            skArc(sketch, "E39.2.13", {"start": v(-71.93, 68.86) * mm, "mid": v(-76.56, 63.67) * mm, "end": v(-80.81, 58.17) * mm});
            skLineSegment(sketch, "E39.2.14", {"start": v(-62.85, 31) * mm, "end": v(-89.3, 44.04) * mm});
            skArc(sketch, "E39.2.15", {"start": v(-14.29, 98.54) * mm, "mid": v(-21.13, 97.3) * mm, "end": v(-27.87, 95.6) * mm});
            skArc(sketch, "E39.2.16", {"start": v(-45.6, 88.52) * mm, "mid": v(-51.66, 85.13) * mm, "end": v(-57.47, 81.32) * mm});
            skArc(sketch, "E39.2.17", {"start": v(-30.36, 94.83) * mm, "mid": v(-36.9, 92.49) * mm, "end": v(-43.26, 89.69) * mm});
            skLineSegment(sketch, "E39.2.18", {"start": v(-19.61, 67.28) * mm, "end": v(-27.87, 95.6) * mm});
            skArc(sketch, "E39.2.19", {"start": v(-41.93, 56.15) * mm, "mid": v(-45.75, 53.09) * mm, "end": v(-49.34, 49.77) * mm});
            skArc(sketch, "E39.2.20", {"start": v(-32.09, 62.3) * mm, "mid": v(-36.36, 59.91) * mm, "end": v(-40.45, 57.23) * mm});
            skArc(sketch, "E39.2.21", {"start": v(-10.05, 69.35) * mm, "mid": v(-14.87, 68.48) * mm, "end": v(-19.61, 67.28) * mm});
            skArc(sketch, "E39.2.22", {"start": v(-50.62, 48.46) * mm, "mid": v(-53.88, 44.81) * mm, "end": v(-56.88, 40.94) * mm});
            skArc(sketch, "E39.2.23", {"start": v(-21.37, 66.74) * mm, "mid": v(-25.97, 65.1) * mm, "end": v(-30.45, 63.12) * mm});
            skLineSegment(sketch, "E39.3.0", {"start": v(-66.36, -22.53) * mm, "end": v(-94.29, -32) * mm});
            skLineSegment(sketch, "E39.3.1", {"start": v(-69.17, -11.27) * mm, "end": v(-98.28, -16) * mm});
            skLineSegment(sketch, "E39.3.2", {"start": v(-69.44, -9.45) * mm, "end": v(-98.66, -13.43) * mm});
            skLineSegment(sketch, "E39.3.3", {"start": v(-62.58, -31.54) * mm, "end": v(-88.92, -44.82) * mm});
            skLineSegment(sketch, "E39.3.4", {"start": v(-66.93, -20.78) * mm, "end": v(-95.1, -29.53) * mm});
            skLineSegment(sketch, "E39.3.5", {"start": v(-61.73, -33.17) * mm, "end": v(-87.71, -47.13) * mm});
            skLineSegment(sketch, "E39.3.6", {"start": v(-56.51, -41.44) * mm, "end": v(-80.3, -58.88) * mm});
            skArc(sketch, "E39.3.7", {"start": v(-55.41, -42.9) * mm, "mid": v(-52.28, -46.67) * mm, "end": v(-48.9, -50.2) * mm});
            skLineSegment(sketch, "E39.3.8", {"start": v(-70.08, 0.3) * mm, "end": v(-99.57, 0.43) * mm});
            skArc(sketch, "E39.3.9", {"start": v(-94.29, -32) * mm, "mid": v(-91.83, -38.5) * mm, "end": v(-88.92, -44.82) * mm});
            skLineSegment(sketch, "E39.3.10", {"start": v(-55.41, -42.9) * mm, "end": v(-78.73, -60.96) * mm});
            skArc(sketch, "E39.3.11", {"start": v(-78.73, -60.96) * mm, "mid": v(-74.29, -66.3) * mm, "end": v(-69.48, -71.33) * mm});
            skLineSegment(sketch, "E39.3.12", {"start": v(-69.07, 11.87) * mm, "end": v(-98.14, 16.86) * mm});
            skArc(sketch, "E39.3.13", {"start": v(-87.71, -47.13) * mm, "mid": v(-84.21, -53.14) * mm, "end": v(-80.3, -58.88) * mm});
            skLineSegment(sketch, "E39.3.14", {"start": v(-48.9, -50.2) * mm, "end": v(-69.48, -71.33) * mm});
            skArc(sketch, "E39.3.15", {"start": v(-98.14, 16.86) * mm, "mid": v(-99.07, 9.98) * mm, "end": v(-99.53, 3.04) * mm});
            skArc(sketch, "E39.3.16", {"start": v(-98.28, -16) * mm, "mid": v(-96.92, -22.82) * mm, "end": v(-95.1, -29.53) * mm});
            skArc(sketch, "E39.3.17", {"start": v(-99.57, 0.43) * mm, "mid": v(-99.36, -6.51) * mm, "end": v(-98.66, -13.43) * mm});
            skLineSegment(sketch, "E39.3.18", {"start": v(-70.05, 2.14) * mm, "end": v(-99.53, 3.04) * mm});
            skArc(sketch, "E39.3.19", {"start": v(-66.36, -22.53) * mm, "mid": v(-64.63, -27.1) * mm, "end": v(-62.58, -31.54) * mm});
            skArc(sketch, "E39.3.20", {"start": v(-69.17, -11.27) * mm, "mid": v(-68.21, -16.06) * mm, "end": v(-66.93, -20.78) * mm});
            skArc(sketch, "E39.3.21", {"start": v(-69.07, 11.87) * mm, "mid": v(-69.73, 7.02) * mm, "end": v(-70.05, 2.14) * mm});
            skArc(sketch, "E39.3.22", {"start": v(-61.73, -33.17) * mm, "mid": v(-59.27, -37.4) * mm, "end": v(-56.51, -41.44) * mm});
            skArc(sketch, "E39.3.23", {"start": v(-70.08, 0.3) * mm, "mid": v(-69.93, -4.58) * mm, "end": v(-69.44, -9.45) * mm});
            skSolve(sketch);
        }
        {
            var Q0;
            Q0=makeQuery(id+"F3.imprint","IMPRINT",FACE,{"disambiguationData":[TD([[makeQuery(id+"F3.imprint","IMPRINT",EDGE,{"derivedFrom":sQuery(id+"F3.wireOp",EDGE,"E39.3.7")}),-1.0]])]});
            var Q1;
            Q1=makeQuery(id+"F3.imprint","IMPRINT",FACE,{"disambiguationData":[TD([[makeQuery(id+"F3.imprint","IMPRINT",EDGE,{"derivedFrom":sQuery(id+"F3.wireOp",EDGE,"E39.3.5")}),1.0]])]});
            var Q2;
            Q2=makeQuery(id+"F3.imprint","IMPRINT",FACE,{"disambiguationData":[TD([[makeQuery(id+"F3.imprint","IMPRINT",EDGE,{"derivedFrom":sQuery(id+"F3.wireOp",EDGE,"E39.3.1")}),1.0]])]});
            var Q3;
            Q3=makeQuery(id+"F3.imprint","IMPRINT",FACE,{"disambiguationData":[TD([[makeQuery(id+"F3.imprint","IMPRINT",EDGE,{"derivedFrom":sQuery(id+"F3.wireOp",EDGE,"E39.3.2")}),-1.0]])]});
            var Q4;
            Q4=makeQuery(id+"F3.imprint","IMPRINT",FACE,{"disambiguationData":[TD([[makeQuery(id+"F3.imprint","IMPRINT",EDGE,{"derivedFrom":sQuery(id+"F3.wireOp",EDGE,"E39.3.12")}),1.0]])]});
            var Q5;
            Q5=makeQuery(id+"F3.imprint","IMPRINT",FACE,{"disambiguationData":[TD([[makeQuery(id+"F3.imprint","IMPRINT",EDGE,{"derivedFrom":sQuery(id+"F3.wireOp",EDGE,"E39.2.7")}),-1.0]])]});
            var Q6;
            Q6=makeQuery(id+"F3.imprint","IMPRINT",FACE,{"disambiguationData":[TD([[makeQuery(id+"F3.imprint","IMPRINT",EDGE,{"derivedFrom":sQuery(id+"F3.wireOp",EDGE,"E39.2.5")}),1.0]])]});
            var Q7;
            Q7=makeQuery(id+"F3.imprint","IMPRINT",FACE,{"disambiguationData":[TD([[makeQuery(id+"F3.imprint","IMPRINT",EDGE,{"derivedFrom":sQuery(id+"F3.wireOp",EDGE,"E39.2.1")}),1.0]])]});
            var Q8;
            Q8=makeQuery(id+"F3.imprint","IMPRINT",FACE,{"disambiguationData":[TD([[makeQuery(id+"F3.imprint","IMPRINT",EDGE,{"derivedFrom":sQuery(id+"F3.wireOp",EDGE,"E39.2.2")}),-1.0]])]});
            var Q9;
            Q9=makeQuery(id+"F3.imprint","IMPRINT",FACE,{"disambiguationData":[TD([[makeQuery(id+"F3.imprint","IMPRINT",EDGE,{"derivedFrom":sQuery(id+"F3.wireOp",EDGE,"E39.2.12")}),1.0]])]});
            var Q10;
            Q10=makeQuery(id+"F3.imprint","IMPRINT",FACE,{"disambiguationData":[TD([[makeQuery(id+"F3.imprint","IMPRINT",EDGE,{"derivedFrom":sQuery(id+"F3.wireOp",EDGE,"E39.1.7")}),-1.0]])]});
            var Q11;
            Q11=makeQuery(id+"F3.imprint","IMPRINT",FACE,{"disambiguationData":[TD([[makeQuery(id+"F3.imprint","IMPRINT",EDGE,{"derivedFrom":sQuery(id+"F3.wireOp",EDGE,"E39.1.5")}),1.0]])]});
            var Q12;
            Q12=makeQuery(id+"F3.imprint","IMPRINT",FACE,{"disambiguationData":[TD([[makeQuery(id+"F3.imprint","IMPRINT",EDGE,{"derivedFrom":sQuery(id+"F3.wireOp",EDGE,"E39.1.1")}),1.0]])]});
            var Q13;
            Q13=makeQuery(id+"F3.imprint","IMPRINT",FACE,{"disambiguationData":[TD([[makeQuery(id+"F3.imprint","IMPRINT",EDGE,{"derivedFrom":sQuery(id+"F3.wireOp",EDGE,"E39.1.2")}),-1.0]])]});
            var Q14;
            Q14=makeQuery(id+"F3.imprint","IMPRINT",FACE,{"disambiguationData":[TD([[makeQuery(id+"F3.imprint","IMPRINT",EDGE,{"derivedFrom":sQuery(id+"F3.wireOp",EDGE,"E39.1.12")}),1.0]])]});
            var Q15;
            Q15=makeQuery(id+"F3.imprint","IMPRINT",FACE,{"disambiguationData":[TD([[makeQuery(id+"F3.imprint","IMPRINT",EDGE,{"derivedFrom":sQuery(id+"F3.wireOp",EDGE,"E17")}),-1.0]])]});
            var Q16;
            Q16=makeQuery(id+"F3.imprint","IMPRINT",FACE,{"disambiguationData":[TD([[makeQuery(id+"F3.imprint","IMPRINT",EDGE,{"derivedFrom":sQuery(id+"F3.wireOp",EDGE,"E20")}),-1.0]])]});
            var Q17;
            Q17=makeQuery(id+"F3.imprint","IMPRINT",FACE,{"disambiguationData":[TD([[makeQuery(id+"F3.imprint","IMPRINT",EDGE,{"derivedFrom":sQuery(id+"F3.wireOp",EDGE,"E26")}),-1.0]])]});
            var Q18;
            Q18=makeQuery(id+"F3.imprint","IMPRINT",FACE,{"disambiguationData":[TD([[makeQuery(id+"F3.imprint","IMPRINT",EDGE,{"derivedFrom":sQuery(id+"F3.wireOp",EDGE,"E15")}),1.0]])]});
            var Q19;
            Q19=makeQuery(id+"F3.imprint","IMPRINT",FACE,{"disambiguationData":[TD([[makeQuery(id+"F3.imprint","IMPRINT",EDGE,{"derivedFrom":sQuery(id+"F3.wireOp",EDGE,"E24")}),-1.0]])]});
            extrude(context, id + "F4", {"entities" : qUnion([Q0, Q1, Q2, Q3, Q4, Q5, Q6, Q7, Q8, Q9, Q10, Q11, Q12, Q13, Q14, Q15, Q16, Q17, Q18, Q19]), "operationType" : NewBodyOperationType.REMOVE, "oppositeDirection" : true, "depth" : 4.5 * mm});
        }
        {
            var Q0;
            Q0=makeQuery(id+"F3.imprint","IMPRINT",FACE,{"disambiguationData":[TD([[makeQuery(id+"F3.imprint","IMPRINT",EDGE,{"derivedFrom":sQuery(id+"F3.wireOp",EDGE,"E39.3.0")}),1.0]])]});
            var Q1;
            Q1=makeQuery(id+"F3.imprint","IMPRINT",FACE,{"disambiguationData":[TD([[makeQuery(id+"F3.imprint","IMPRINT",EDGE,{"derivedFrom":sQuery(id+"F3.wireOp",EDGE,"E39.2.0")}),1.0]])]});
            var Q2;
            Q2=makeQuery(id+"F3.imprint","IMPRINT",FACE,{"disambiguationData":[TD([[makeQuery(id+"F3.imprint","IMPRINT",EDGE,{"derivedFrom":sQuery(id+"F3.wireOp",EDGE,"E39.1.0")}),1.0]])]});
            var Q3;
            Q3=makeQuery(id+"F3.imprint","IMPRINT",FACE,{"disambiguationData":[TD([[makeQuery(id+"F3.imprint","IMPRINT",EDGE,{"derivedFrom":sQuery(id+"F3.wireOp",EDGE,"E22")}),-1.0]])]});
            extrude(context, id + "F5", {"entities" : qUnion([Q0, Q1, Q2, Q3]), "operationType" : NewBodyOperationType.REMOVE, "oppositeDirection" : true, "depth" : 2 * mm});
        }
        {
            var Q0;
            Q0=makeQuery(id+"F4.boolean.opBoolean","COPY",EDGE,{"derivedFrom":makeQuery(id+"F4.opExtrude","SWEPT_EDGE",EDGE,{"disambiguationData":[OSD([sQuery(id+"F3.wireOp",EDGE,"E39.3.7"),sQuery(id+"F3.wireOp",EDGE,"E39.3.10")])]})});
            var Q1;
            Q1=makeQuery(id+"F4.boolean.opBoolean","COPY",EDGE,{"derivedFrom":makeQuery(id+"F4.opExtrude","SWEPT_EDGE",EDGE,{"disambiguationData":[OSD([sQuery(id+"F3.wireOp",EDGE,"E39.3.5"),sQuery(id+"F3.wireOp",EDGE,"E39.3.22")])]})});
            var Q2;
            Q2=makeQuery(id+"F5.boolean.opBoolean","COPY",EDGE,{"derivedFrom":makeQuery(id+"F5.opExtrude","SWEPT_EDGE",EDGE,{"disambiguationData":[OSD([sQuery(id+"F3.wireOp",EDGE,"E39.3.0"),sQuery(id+"F3.wireOp",EDGE,"E39.3.19")])]})});
            var Q3;
            Q3=makeQuery(id+"F4.boolean.opBoolean","COPY",EDGE,{"derivedFrom":makeQuery(id+"F4.opExtrude","SWEPT_EDGE",EDGE,{"disambiguationData":[OSD([sQuery(id+"F3.wireOp",EDGE,"E39.3.1"),sQuery(id+"F3.wireOp",EDGE,"E39.3.20")])]})});
            var Q4;
            Q4=makeQuery(id+"F4.boolean.opBoolean","COPY",EDGE,{"derivedFrom":makeQuery(id+"F4.opExtrude","SWEPT_EDGE",EDGE,{"disambiguationData":[OSD([sQuery(id+"F3.wireOp",EDGE,"E39.3.8"),sQuery(id+"F3.wireOp",EDGE,"E39.3.23")])]})});
            var Q5;
            Q5=makeQuery(id+"F4.boolean.opBoolean","COPY",EDGE,{"derivedFrom":makeQuery(id+"F4.opExtrude","SWEPT_EDGE",EDGE,{"disambiguationData":[OSD([sQuery(id+"F3.wireOp",EDGE,"E39.3.12"),sQuery(id+"F3.wireOp",EDGE,"E39.3.21")])]})});
            var Q6;
            Q6=makeQuery(id+"F4.boolean.opBoolean","COPY",EDGE,{"derivedFrom":makeQuery(id+"F4.opExtrude","SWEPT_EDGE",EDGE,{"disambiguationData":[OSD([sQuery(id+"F3.wireOp",EDGE,"E39.3.7"),sQuery(id+"F3.wireOp",EDGE,"E39.3.14")])]})});
            var Q7;
            Q7=makeQuery(id+"F4.boolean.opBoolean","COPY",EDGE,{"derivedFrom":makeQuery(id+"F4.opExtrude","SWEPT_EDGE",EDGE,{"disambiguationData":[OSD([sQuery(id+"F3.wireOp",EDGE,"E39.3.6"),sQuery(id+"F3.wireOp",EDGE,"E39.3.22")])]})});
            var Q8;
            Q8=makeQuery(id+"F5.boolean.opBoolean","COPY",EDGE,{"derivedFrom":makeQuery(id+"F5.opExtrude","SWEPT_EDGE",EDGE,{"disambiguationData":[OSD([sQuery(id+"F3.wireOp",EDGE,"E39.3.3"),sQuery(id+"F3.wireOp",EDGE,"E39.3.19")])]})});
            var Q9;
            Q9=makeQuery(id+"F4.boolean.opBoolean","COPY",EDGE,{"derivedFrom":makeQuery(id+"F4.opExtrude","SWEPT_EDGE",EDGE,{"disambiguationData":[OSD([sQuery(id+"F3.wireOp",EDGE,"E39.3.4"),sQuery(id+"F3.wireOp",EDGE,"E39.3.20")])]})});
            var Q10;
            Q10=makeQuery(id+"F4.boolean.opBoolean","COPY",EDGE,{"derivedFrom":makeQuery(id+"F4.opExtrude","SWEPT_EDGE",EDGE,{"disambiguationData":[OSD([sQuery(id+"F3.wireOp",EDGE,"E39.3.2"),sQuery(id+"F3.wireOp",EDGE,"E39.3.23")])]})});
            var Q11;
            Q11=makeQuery(id+"F4.boolean.opBoolean","COPY",EDGE,{"derivedFrom":makeQuery(id+"F4.opExtrude","SWEPT_EDGE",EDGE,{"disambiguationData":[OSD([sQuery(id+"F3.wireOp",EDGE,"E39.3.18"),sQuery(id+"F3.wireOp",EDGE,"E39.3.21")])]})});
            var Q12;
            Q12=makeQuery(id+"F4.boolean.opBoolean","COPY",EDGE,{"derivedFrom":makeQuery(id+"F4.opExtrude","SWEPT_EDGE",EDGE,{"disambiguationData":[OSD([sQuery(id+"F3.wireOp",EDGE,"E39.3.12"),sQuery(id+"F3.wireOp",EDGE,"E39.3.15")])]})});
            var Q13;
            Q13=makeQuery(id+"F4.boolean.opBoolean","COPY",EDGE,{"derivedFrom":makeQuery(id+"F4.opExtrude","SWEPT_EDGE",EDGE,{"disambiguationData":[OSD([sQuery(id+"F3.wireOp",EDGE,"E39.3.8"),sQuery(id+"F3.wireOp",EDGE,"E39.3.17")])]})});
            var Q14;
            Q14=makeQuery(id+"F4.boolean.opBoolean","COPY",EDGE,{"derivedFrom":makeQuery(id+"F4.opExtrude","SWEPT_EDGE",EDGE,{"disambiguationData":[OSD([sQuery(id+"F3.wireOp",EDGE,"E39.3.1"),sQuery(id+"F3.wireOp",EDGE,"E39.3.16")])]})});
            var Q15;
            Q15=makeQuery(id+"F5.boolean.opBoolean","COPY",EDGE,{"derivedFrom":makeQuery(id+"F5.opExtrude","SWEPT_EDGE",EDGE,{"disambiguationData":[OSD([sQuery(id+"F3.wireOp",EDGE,"E39.3.0"),sQuery(id+"F3.wireOp",EDGE,"E39.3.9")])]})});
            var Q16;
            Q16=makeQuery(id+"F4.boolean.opBoolean","COPY",EDGE,{"derivedFrom":makeQuery(id+"F4.opExtrude","SWEPT_EDGE",EDGE,{"disambiguationData":[OSD([sQuery(id+"F3.wireOp",EDGE,"E39.3.5"),sQuery(id+"F3.wireOp",EDGE,"E39.3.13")])]})});
            var Q17;
            Q17=makeQuery(id+"F4.boolean.opBoolean","COPY",EDGE,{"derivedFrom":makeQuery(id+"F4.opExtrude","SWEPT_EDGE",EDGE,{"disambiguationData":[OSD([sQuery(id+"F3.wireOp",EDGE,"E39.3.10"),sQuery(id+"F3.wireOp",EDGE,"E39.3.11")])]})});
            var Q18;
            Q18=makeQuery(id+"F4.boolean.opBoolean","COPY",EDGE,{"derivedFrom":makeQuery(id+"F4.opExtrude","SWEPT_EDGE",EDGE,{"disambiguationData":[OSD([sQuery(id+"F3.wireOp",EDGE,"E39.3.11"),sQuery(id+"F3.wireOp",EDGE,"E39.3.14")])]})});
            var Q19;
            Q19=makeQuery(id+"F4.boolean.opBoolean","COPY",EDGE,{"derivedFrom":makeQuery(id+"F4.opExtrude","SWEPT_EDGE",EDGE,{"disambiguationData":[OSD([sQuery(id+"F3.wireOp",EDGE,"E39.3.6"),sQuery(id+"F3.wireOp",EDGE,"E39.3.13")])]})});
            var Q20;
            Q20=makeQuery(id+"F5.boolean.opBoolean","COPY",EDGE,{"derivedFrom":makeQuery(id+"F5.opExtrude","SWEPT_EDGE",EDGE,{"disambiguationData":[OSD([sQuery(id+"F3.wireOp",EDGE,"E39.3.3"),sQuery(id+"F3.wireOp",EDGE,"E39.3.9")])]})});
            var Q21;
            Q21=makeQuery(id+"F4.boolean.opBoolean","COPY",EDGE,{"derivedFrom":makeQuery(id+"F4.opExtrude","SWEPT_EDGE",EDGE,{"disambiguationData":[OSD([sQuery(id+"F3.wireOp",EDGE,"E39.3.4"),sQuery(id+"F3.wireOp",EDGE,"E39.3.16")])]})});
            var Q22;
            Q22=makeQuery(id+"F4.boolean.opBoolean","COPY",EDGE,{"derivedFrom":makeQuery(id+"F4.opExtrude","SWEPT_EDGE",EDGE,{"disambiguationData":[OSD([sQuery(id+"F3.wireOp",EDGE,"E39.3.2"),sQuery(id+"F3.wireOp",EDGE,"E39.3.17")])]})});
            var Q23;
            Q23=makeQuery(id+"F4.boolean.opBoolean","COPY",EDGE,{"derivedFrom":makeQuery(id+"F4.opExtrude","SWEPT_EDGE",EDGE,{"disambiguationData":[OSD([sQuery(id+"F3.wireOp",EDGE,"E39.3.15"),sQuery(id+"F3.wireOp",EDGE,"E39.3.18")])]})});
            var Q24;
            Q24=makeQuery(id+"F4.boolean.opBoolean","COPY",EDGE,{"derivedFrom":makeQuery(id+"F4.opExtrude","SWEPT_EDGE",EDGE,{"disambiguationData":[OSD([sQuery(id+"F3.wireOp",EDGE,"E39.2.7"),sQuery(id+"F3.wireOp",EDGE,"E39.2.14")])]})});
            var Q25;
            Q25=makeQuery(id+"F4.boolean.opBoolean","COPY",EDGE,{"derivedFrom":makeQuery(id+"F4.opExtrude","SWEPT_EDGE",EDGE,{"disambiguationData":[OSD([sQuery(id+"F3.wireOp",EDGE,"E39.2.6"),sQuery(id+"F3.wireOp",EDGE,"E39.2.22")])]})});
            var Q26;
            Q26=makeQuery(id+"F5.boolean.opBoolean","COPY",EDGE,{"derivedFrom":makeQuery(id+"F5.opExtrude","SWEPT_EDGE",EDGE,{"disambiguationData":[OSD([sQuery(id+"F3.wireOp",EDGE,"E39.2.3"),sQuery(id+"F3.wireOp",EDGE,"E39.2.19")])]})});
            var Q27;
            Q27=makeQuery(id+"F4.boolean.opBoolean","COPY",EDGE,{"derivedFrom":makeQuery(id+"F4.opExtrude","SWEPT_EDGE",EDGE,{"disambiguationData":[OSD([sQuery(id+"F3.wireOp",EDGE,"E39.2.4"),sQuery(id+"F3.wireOp",EDGE,"E39.2.20")])]})});
            var Q28;
            Q28=makeQuery(id+"F4.boolean.opBoolean","COPY",EDGE,{"derivedFrom":makeQuery(id+"F4.opExtrude","SWEPT_EDGE",EDGE,{"disambiguationData":[OSD([sQuery(id+"F3.wireOp",EDGE,"E39.2.2"),sQuery(id+"F3.wireOp",EDGE,"E39.2.23")])]})});
            var Q29;
            Q29=makeQuery(id+"F4.boolean.opBoolean","COPY",EDGE,{"derivedFrom":makeQuery(id+"F4.opExtrude","SWEPT_EDGE",EDGE,{"disambiguationData":[OSD([sQuery(id+"F3.wireOp",EDGE,"E39.2.18"),sQuery(id+"F3.wireOp",EDGE,"E39.2.21")])]})});
            var Q30;
            Q30=makeQuery(id+"F4.boolean.opBoolean","COPY",EDGE,{"derivedFrom":makeQuery(id+"F4.opExtrude","SWEPT_EDGE",EDGE,{"disambiguationData":[OSD([sQuery(id+"F3.wireOp",EDGE,"E39.2.7"),sQuery(id+"F3.wireOp",EDGE,"E39.2.10")])]})});
            var Q31;
            Q31=makeQuery(id+"F4.boolean.opBoolean","COPY",EDGE,{"derivedFrom":makeQuery(id+"F4.opExtrude","SWEPT_EDGE",EDGE,{"disambiguationData":[OSD([sQuery(id+"F3.wireOp",EDGE,"E39.2.5"),sQuery(id+"F3.wireOp",EDGE,"E39.2.22")])]})});
            var Q32;
            Q32=makeQuery(id+"F5.boolean.opBoolean","COPY",EDGE,{"derivedFrom":makeQuery(id+"F5.opExtrude","SWEPT_EDGE",EDGE,{"disambiguationData":[OSD([sQuery(id+"F3.wireOp",EDGE,"E39.2.0"),sQuery(id+"F3.wireOp",EDGE,"E39.2.19")])]})});
            var Q33;
            Q33=makeQuery(id+"F4.boolean.opBoolean","COPY",EDGE,{"derivedFrom":makeQuery(id+"F4.opExtrude","SWEPT_EDGE",EDGE,{"disambiguationData":[OSD([sQuery(id+"F3.wireOp",EDGE,"E39.2.1"),sQuery(id+"F3.wireOp",EDGE,"E39.2.20")])]})});
            var Q34;
            Q34=makeQuery(id+"F4.boolean.opBoolean","COPY",EDGE,{"derivedFrom":makeQuery(id+"F4.opExtrude","SWEPT_EDGE",EDGE,{"disambiguationData":[OSD([sQuery(id+"F3.wireOp",EDGE,"E39.2.8"),sQuery(id+"F3.wireOp",EDGE,"E39.2.23")])]})});
            var Q35;
            Q35=makeQuery(id+"F4.boolean.opBoolean","COPY",EDGE,{"derivedFrom":makeQuery(id+"F4.opExtrude","SWEPT_EDGE",EDGE,{"disambiguationData":[OSD([sQuery(id+"F3.wireOp",EDGE,"E39.2.12"),sQuery(id+"F3.wireOp",EDGE,"E39.2.21")])]})});
            var Q36;
            Q36=makeQuery(id+"F4.boolean.opBoolean","COPY",EDGE,{"derivedFrom":makeQuery(id+"F4.opExtrude","SWEPT_EDGE",EDGE,{"disambiguationData":[OSD([sQuery(id+"F3.wireOp",EDGE,"E39.2.11"),sQuery(id+"F3.wireOp",EDGE,"E39.2.14")])]})});
            var Q37;
            Q37=makeQuery(id+"F4.boolean.opBoolean","COPY",EDGE,{"derivedFrom":makeQuery(id+"F4.opExtrude","SWEPT_EDGE",EDGE,{"disambiguationData":[OSD([sQuery(id+"F3.wireOp",EDGE,"E39.2.6"),sQuery(id+"F3.wireOp",EDGE,"E39.2.13")])]})});
            var Q38;
            Q38=makeQuery(id+"F5.boolean.opBoolean","COPY",EDGE,{"derivedFrom":makeQuery(id+"F5.opExtrude","SWEPT_EDGE",EDGE,{"disambiguationData":[OSD([sQuery(id+"F3.wireOp",EDGE,"E39.2.3"),sQuery(id+"F3.wireOp",EDGE,"E39.2.9")])]})});
            var Q39;
            Q39=makeQuery(id+"F4.boolean.opBoolean","COPY",EDGE,{"derivedFrom":makeQuery(id+"F4.opExtrude","SWEPT_EDGE",EDGE,{"disambiguationData":[OSD([sQuery(id+"F3.wireOp",EDGE,"E39.2.4"),sQuery(id+"F3.wireOp",EDGE,"E39.2.16")])]})});
            var Q40;
            Q40=makeQuery(id+"F4.boolean.opBoolean","COPY",EDGE,{"derivedFrom":makeQuery(id+"F4.opExtrude","SWEPT_EDGE",EDGE,{"disambiguationData":[OSD([sQuery(id+"F3.wireOp",EDGE,"E39.2.2"),sQuery(id+"F3.wireOp",EDGE,"E39.2.17")])]})});
            var Q41;
            Q41=makeQuery(id+"F4.boolean.opBoolean","COPY",EDGE,{"derivedFrom":makeQuery(id+"F4.opExtrude","SWEPT_EDGE",EDGE,{"disambiguationData":[OSD([sQuery(id+"F3.wireOp",EDGE,"E39.2.15"),sQuery(id+"F3.wireOp",EDGE,"E39.2.18")])]})});
            var Q42;
            Q42=makeQuery(id+"F4.boolean.opBoolean","COPY",EDGE,{"derivedFrom":makeQuery(id+"F4.opExtrude","SWEPT_EDGE",EDGE,{"disambiguationData":[OSD([sQuery(id+"F3.wireOp",EDGE,"E39.2.10"),sQuery(id+"F3.wireOp",EDGE,"E39.2.11")])]})});
            var Q43;
            Q43=makeQuery(id+"F4.boolean.opBoolean","COPY",EDGE,{"derivedFrom":makeQuery(id+"F4.opExtrude","SWEPT_EDGE",EDGE,{"disambiguationData":[OSD([sQuery(id+"F3.wireOp",EDGE,"E39.2.5"),sQuery(id+"F3.wireOp",EDGE,"E39.2.13")])]})});
            var Q44;
            Q44=makeQuery(id+"F5.boolean.opBoolean","COPY",EDGE,{"derivedFrom":makeQuery(id+"F5.opExtrude","SWEPT_EDGE",EDGE,{"disambiguationData":[OSD([sQuery(id+"F3.wireOp",EDGE,"E39.2.0"),sQuery(id+"F3.wireOp",EDGE,"E39.2.9")])]})});
            var Q45;
            Q45=makeQuery(id+"F4.boolean.opBoolean","COPY",EDGE,{"derivedFrom":makeQuery(id+"F4.opExtrude","SWEPT_EDGE",EDGE,{"disambiguationData":[OSD([sQuery(id+"F3.wireOp",EDGE,"E39.2.1"),sQuery(id+"F3.wireOp",EDGE,"E39.2.16")])]})});
            var Q46;
            Q46=makeQuery(id+"F4.boolean.opBoolean","COPY",EDGE,{"derivedFrom":makeQuery(id+"F4.opExtrude","SWEPT_EDGE",EDGE,{"disambiguationData":[OSD([sQuery(id+"F3.wireOp",EDGE,"E39.2.8"),sQuery(id+"F3.wireOp",EDGE,"E39.2.17")])]})});
            var Q47;
            Q47=makeQuery(id+"F4.boolean.opBoolean","COPY",EDGE,{"derivedFrom":makeQuery(id+"F4.opExtrude","SWEPT_EDGE",EDGE,{"disambiguationData":[OSD([sQuery(id+"F3.wireOp",EDGE,"E39.2.12"),sQuery(id+"F3.wireOp",EDGE,"E39.2.15")])]})});
            var Q48;
            Q48=makeQuery(id+"F4.boolean.opBoolean","COPY",EDGE,{"derivedFrom":makeQuery(id+"F4.opExtrude","SWEPT_EDGE",EDGE,{"disambiguationData":[OSD([sQuery(id+"F3.wireOp",EDGE,"E39.1.7"),sQuery(id+"F3.wireOp",EDGE,"E39.1.14")])]})});
            var Q49;
            Q49=makeQuery(id+"F4.boolean.opBoolean","COPY",EDGE,{"derivedFrom":makeQuery(id+"F4.opExtrude","SWEPT_EDGE",EDGE,{"disambiguationData":[OSD([sQuery(id+"F3.wireOp",EDGE,"E39.1.6"),sQuery(id+"F3.wireOp",EDGE,"E39.1.22")])]})});
            var Q50;
            Q50=makeQuery(id+"F5.boolean.opBoolean","COPY",EDGE,{"derivedFrom":makeQuery(id+"F5.opExtrude","SWEPT_EDGE",EDGE,{"disambiguationData":[OSD([sQuery(id+"F3.wireOp",EDGE,"E39.1.3"),sQuery(id+"F3.wireOp",EDGE,"E39.1.19")])]})});
            var Q51;
            Q51=makeQuery(id+"F4.boolean.opBoolean","COPY",EDGE,{"derivedFrom":makeQuery(id+"F4.opExtrude","SWEPT_EDGE",EDGE,{"disambiguationData":[OSD([sQuery(id+"F3.wireOp",EDGE,"E39.1.4"),sQuery(id+"F3.wireOp",EDGE,"E39.1.20")])]})});
            var Q52;
            Q52=makeQuery(id+"F4.boolean.opBoolean","COPY",EDGE,{"derivedFrom":makeQuery(id+"F4.opExtrude","SWEPT_EDGE",EDGE,{"disambiguationData":[OSD([sQuery(id+"F3.wireOp",EDGE,"E39.1.18"),sQuery(id+"F3.wireOp",EDGE,"E39.1.21")])]})});
            var Q53;
            Q53=makeQuery(id+"F4.boolean.opBoolean","COPY",EDGE,{"derivedFrom":makeQuery(id+"F4.opExtrude","SWEPT_EDGE",EDGE,{"disambiguationData":[OSD([sQuery(id+"F3.wireOp",EDGE,"E39.1.2"),sQuery(id+"F3.wireOp",EDGE,"E39.1.23")])]})});
            var Q54;
            Q54=makeQuery(id+"F4.boolean.opBoolean","COPY",EDGE,{"derivedFrom":makeQuery(id+"F4.opExtrude","SWEPT_EDGE",EDGE,{"disambiguationData":[OSD([sQuery(id+"F3.wireOp",EDGE,"E39.1.7"),sQuery(id+"F3.wireOp",EDGE,"E39.1.10")])]})});
            var Q55;
            Q55=makeQuery(id+"F4.boolean.opBoolean","COPY",EDGE,{"derivedFrom":makeQuery(id+"F4.opExtrude","SWEPT_EDGE",EDGE,{"disambiguationData":[OSD([sQuery(id+"F3.wireOp",EDGE,"E39.1.5"),sQuery(id+"F3.wireOp",EDGE,"E39.1.22")])]})});
            var Q56;
            Q56=makeQuery(id+"F5.boolean.opBoolean","COPY",EDGE,{"derivedFrom":makeQuery(id+"F5.opExtrude","SWEPT_EDGE",EDGE,{"disambiguationData":[OSD([sQuery(id+"F3.wireOp",EDGE,"E39.1.0"),sQuery(id+"F3.wireOp",EDGE,"E39.1.19")])]})});
            var Q57;
            Q57=makeQuery(id+"F4.boolean.opBoolean","COPY",EDGE,{"derivedFrom":makeQuery(id+"F4.opExtrude","SWEPT_EDGE",EDGE,{"disambiguationData":[OSD([sQuery(id+"F3.wireOp",EDGE,"E39.1.1"),sQuery(id+"F3.wireOp",EDGE,"E39.1.20")])]})});
            var Q58;
            Q58=makeQuery(id+"F4.boolean.opBoolean","COPY",EDGE,{"derivedFrom":makeQuery(id+"F4.opExtrude","SWEPT_EDGE",EDGE,{"disambiguationData":[OSD([sQuery(id+"F3.wireOp",EDGE,"E39.1.8"),sQuery(id+"F3.wireOp",EDGE,"E39.1.23")])]})});
            var Q59;
            Q59=makeQuery(id+"F4.boolean.opBoolean","COPY",EDGE,{"derivedFrom":makeQuery(id+"F4.opExtrude","SWEPT_EDGE",EDGE,{"disambiguationData":[OSD([sQuery(id+"F3.wireOp",EDGE,"E39.1.12"),sQuery(id+"F3.wireOp",EDGE,"E39.1.21")])]})});
            var Q60;
            Q60=makeQuery(id+"F4.boolean.opBoolean","COPY",EDGE,{"derivedFrom":makeQuery(id+"F4.opExtrude","SWEPT_EDGE",EDGE,{"disambiguationData":[OSD([sQuery(id+"F3.wireOp",EDGE,"E39.1.11"),sQuery(id+"F3.wireOp",EDGE,"E39.1.14")])]})});
            var Q61;
            Q61=makeQuery(id+"F4.boolean.opBoolean","COPY",EDGE,{"derivedFrom":makeQuery(id+"F4.opExtrude","SWEPT_EDGE",EDGE,{"disambiguationData":[OSD([sQuery(id+"F3.wireOp",EDGE,"E39.1.6"),sQuery(id+"F3.wireOp",EDGE,"E39.1.13")])]})});
            var Q62;
            Q62=makeQuery(id+"F5.boolean.opBoolean","COPY",EDGE,{"derivedFrom":makeQuery(id+"F5.opExtrude","SWEPT_EDGE",EDGE,{"disambiguationData":[OSD([sQuery(id+"F3.wireOp",EDGE,"E39.1.3"),sQuery(id+"F3.wireOp",EDGE,"E39.1.9")])]})});
            var Q63;
            Q63=makeQuery(id+"F4.boolean.opBoolean","COPY",EDGE,{"derivedFrom":makeQuery(id+"F4.opExtrude","SWEPT_EDGE",EDGE,{"disambiguationData":[OSD([sQuery(id+"F3.wireOp",EDGE,"E39.1.4"),sQuery(id+"F3.wireOp",EDGE,"E39.1.16")])]})});
            var Q64;
            Q64=makeQuery(id+"F4.boolean.opBoolean","COPY",EDGE,{"derivedFrom":makeQuery(id+"F4.opExtrude","SWEPT_EDGE",EDGE,{"disambiguationData":[OSD([sQuery(id+"F3.wireOp",EDGE,"E39.1.2"),sQuery(id+"F3.wireOp",EDGE,"E39.1.17")])]})});
            var Q65;
            Q65=makeQuery(id+"F4.boolean.opBoolean","COPY",EDGE,{"derivedFrom":makeQuery(id+"F4.opExtrude","SWEPT_EDGE",EDGE,{"disambiguationData":[OSD([sQuery(id+"F3.wireOp",EDGE,"E39.1.15"),sQuery(id+"F3.wireOp",EDGE,"E39.1.18")])]})});
            var Q66;
            Q66=makeQuery(id+"F4.boolean.opBoolean","COPY",EDGE,{"derivedFrom":makeQuery(id+"F4.opExtrude","SWEPT_EDGE",EDGE,{"disambiguationData":[OSD([sQuery(id+"F3.wireOp",EDGE,"E39.1.10"),sQuery(id+"F3.wireOp",EDGE,"E39.1.11")])]})});
            var Q67;
            Q67=makeQuery(id+"F4.boolean.opBoolean","COPY",EDGE,{"derivedFrom":makeQuery(id+"F4.opExtrude","SWEPT_EDGE",EDGE,{"disambiguationData":[OSD([sQuery(id+"F3.wireOp",EDGE,"E39.1.5"),sQuery(id+"F3.wireOp",EDGE,"E39.1.13")])]})});
            var Q68;
            Q68=makeQuery(id+"F5.boolean.opBoolean","COPY",EDGE,{"derivedFrom":makeQuery(id+"F5.opExtrude","SWEPT_EDGE",EDGE,{"disambiguationData":[OSD([sQuery(id+"F3.wireOp",EDGE,"E39.1.0"),sQuery(id+"F3.wireOp",EDGE,"E39.1.9")])]})});
            var Q69;
            Q69=makeQuery(id+"F4.boolean.opBoolean","COPY",EDGE,{"derivedFrom":makeQuery(id+"F4.opExtrude","SWEPT_EDGE",EDGE,{"disambiguationData":[OSD([sQuery(id+"F3.wireOp",EDGE,"E39.1.1"),sQuery(id+"F3.wireOp",EDGE,"E39.1.16")])]})});
            var Q70;
            Q70=makeQuery(id+"F4.boolean.opBoolean","COPY",EDGE,{"derivedFrom":makeQuery(id+"F4.opExtrude","SWEPT_EDGE",EDGE,{"disambiguationData":[OSD([sQuery(id+"F3.wireOp",EDGE,"E39.1.8"),sQuery(id+"F3.wireOp",EDGE,"E39.1.17")])]})});
            var Q71;
            Q71=makeQuery(id+"F4.boolean.opBoolean","COPY",EDGE,{"derivedFrom":makeQuery(id+"F4.opExtrude","SWEPT_EDGE",EDGE,{"disambiguationData":[OSD([sQuery(id+"F3.wireOp",EDGE,"E39.1.12"),sQuery(id+"F3.wireOp",EDGE,"E39.1.15")])]})});
            var Q72;
            Q72=makeQuery(id+"F4.boolean.opBoolean","COPY",EDGE,{"derivedFrom":makeQuery(id+"F4.opExtrude","SWEPT_EDGE",EDGE,{"disambiguationData":[OSD([sQuery(id+"F3.wireOp",EDGE,"E17"),sQuery(id+"F3.wireOp",EDGE,"E31.trimOffspring")])]})});
            var Q73;
            Q73=makeQuery(id+"F4.boolean.opBoolean","COPY",EDGE,{"derivedFrom":makeQuery(id+"F4.opExtrude","SWEPT_EDGE",EDGE,{"disambiguationData":[OSD([sQuery(id+"F3.wireOp",EDGE,"E20"),sQuery(id+"F3.wireOp",EDGE,"E33.trimOffspring")])]})});
            var Q74;
            Q74=makeQuery(id+"F4.boolean.opBoolean","COPY",EDGE,{"derivedFrom":makeQuery(id+"F4.opExtrude","SWEPT_EDGE",EDGE,{"disambiguationData":[OSD([sQuery(id+"F3.wireOp",EDGE,"E15"),sQuery(id+"F3.wireOp",EDGE,"E28")])]})});
            var Q75;
            Q75=makeQuery(id+"F4.boolean.opBoolean","COPY",EDGE,{"derivedFrom":makeQuery(id+"F4.opExtrude","SWEPT_EDGE",EDGE,{"disambiguationData":[OSD([sQuery(id+"F3.wireOp",EDGE,"E26"),sQuery(id+"F3.wireOp",EDGE,"E29.trimOffspring")])]})});
            var Q76;
            Q76=makeQuery(id+"F4.boolean.opBoolean","COPY",EDGE,{"derivedFrom":makeQuery(id+"F4.opExtrude","SWEPT_EDGE",EDGE,{"disambiguationData":[OSD([sQuery(id+"F3.wireOp",EDGE,"E24"),sQuery(id+"F3.wireOp",EDGE,"E30.trimOffspring")])]})});
            var Q77;
            Q77=makeQuery(id+"F5.boolean.opBoolean","COPY",EDGE,{"derivedFrom":makeQuery(id+"F5.opExtrude","SWEPT_EDGE",EDGE,{"disambiguationData":[OSD([sQuery(id+"F3.wireOp",EDGE,"E22"),sQuery(id+"F3.wireOp",EDGE,"E34.trimOffspring")])]})});
            var Q78;
            Q78=makeQuery(id+"F4.boolean.opBoolean","COPY",EDGE,{"derivedFrom":makeQuery(id+"F4.opExtrude","SWEPT_EDGE",EDGE,{"disambiguationData":[OSD([sQuery(id+"F3.wireOp",EDGE,"E15"),sQuery(id+"F3.wireOp",EDGE,"E18")])]})});
            var Q79;
            Q79=makeQuery(id+"F4.boolean.opBoolean","COPY",EDGE,{"derivedFrom":makeQuery(id+"F4.opExtrude","SWEPT_EDGE",EDGE,{"disambiguationData":[OSD([sQuery(id+"F3.wireOp",EDGE,"E27"),sQuery(id+"F3.wireOp",EDGE,"E29.trimOffspring")])]})});
            var Q80;
            Q80=makeQuery(id+"F4.boolean.opBoolean","COPY",EDGE,{"derivedFrom":makeQuery(id+"F4.opExtrude","SWEPT_EDGE",EDGE,{"disambiguationData":[OSD([sQuery(id+"F3.wireOp",EDGE,"E25"),sQuery(id+"F3.wireOp",EDGE,"E30.trimOffspring")])]})});
            var Q81;
            Q81=makeQuery(id+"F5.boolean.opBoolean","COPY",EDGE,{"derivedFrom":makeQuery(id+"F5.opExtrude","SWEPT_EDGE",EDGE,{"disambiguationData":[OSD([sQuery(id+"F3.wireOp",EDGE,"E23"),sQuery(id+"F3.wireOp",EDGE,"E34.trimOffspring")])]})});
            var Q82;
            Q82=makeQuery(id+"F4.boolean.opBoolean","COPY",EDGE,{"derivedFrom":makeQuery(id+"F4.opExtrude","SWEPT_EDGE",EDGE,{"disambiguationData":[OSD([sQuery(id+"F3.wireOp",EDGE,"E21"),sQuery(id+"F3.wireOp",EDGE,"E33.trimOffspring")])]})});
            var Q83;
            Q83=makeQuery(id+"F4.boolean.opBoolean","COPY",EDGE,{"derivedFrom":makeQuery(id+"F4.opExtrude","SWEPT_EDGE",EDGE,{"disambiguationData":[OSD([sQuery(id+"F3.wireOp",EDGE,"E19"),sQuery(id+"F3.wireOp",EDGE,"E31.trimOffspring")])]})});
            var Q84;
            Q84=makeQuery(id+"F4.boolean.opBoolean","COPY",EDGE,{"derivedFrom":makeQuery(id+"F4.opExtrude","SWEPT_EDGE",EDGE,{"disambiguationData":[OSD([sQuery(id+"F3.wireOp",EDGE,"E17"),sQuery(id+"F3.wireOp",EDGE,"E32.trimOffspring")])]})});
            var Q85;
            Q85=makeQuery(id+"F4.boolean.opBoolean","COPY",EDGE,{"derivedFrom":makeQuery(id+"F4.opExtrude","SWEPT_EDGE",EDGE,{"disambiguationData":[OSD([sQuery(id+"F3.wireOp",EDGE,"E20"),sQuery(id+"F3.wireOp",EDGE,"E36.trimOffspring")])]})});
            var Q86;
            Q86=makeQuery(id+"F5.boolean.opBoolean","COPY",EDGE,{"derivedFrom":makeQuery(id+"F5.opExtrude","SWEPT_EDGE",EDGE,{"disambiguationData":[OSD([sQuery(id+"F3.wireOp",EDGE,"E22"),sQuery(id+"F3.wireOp",EDGE,"E35.trimOffspring")])]})});
            var Q87;
            Q87=makeQuery(id+"F4.boolean.opBoolean","COPY",EDGE,{"derivedFrom":makeQuery(id+"F4.opExtrude","SWEPT_EDGE",EDGE,{"disambiguationData":[OSD([sQuery(id+"F3.wireOp",EDGE,"E24"),sQuery(id+"F3.wireOp",EDGE,"E37.trimOffspring")])]})});
            var Q88;
            Q88=makeQuery(id+"F4.boolean.opBoolean","COPY",EDGE,{"derivedFrom":makeQuery(id+"F4.opExtrude","SWEPT_EDGE",EDGE,{"disambiguationData":[OSD([sQuery(id+"F3.wireOp",EDGE,"E26"),sQuery(id+"F3.wireOp",EDGE,"E38.trimOffspring")])]})});
            var Q89;
            Q89=makeQuery(id+"F4.boolean.opBoolean","COPY",EDGE,{"derivedFrom":makeQuery(id+"F4.opExtrude","SWEPT_EDGE",EDGE,{"disambiguationData":[OSD([sQuery(id+"F3.wireOp",EDGE,"E16"),sQuery(id+"F3.wireOp",EDGE,"E28")])]})});
            var Q90;
            Q90=makeQuery(id+"F4.boolean.opBoolean","COPY",EDGE,{"derivedFrom":makeQuery(id+"F4.opExtrude","SWEPT_EDGE",EDGE,{"disambiguationData":[OSD([sQuery(id+"F3.wireOp",EDGE,"E16"),sQuery(id+"F3.wireOp",EDGE,"E18")])]})});
            var Q91;
            Q91=makeQuery(id+"F4.boolean.opBoolean","COPY",EDGE,{"derivedFrom":makeQuery(id+"F4.opExtrude","SWEPT_EDGE",EDGE,{"disambiguationData":[OSD([sQuery(id+"F3.wireOp",EDGE,"E27"),sQuery(id+"F3.wireOp",EDGE,"E38.trimOffspring")])]})});
            var Q92;
            Q92=makeQuery(id+"F4.boolean.opBoolean","COPY",EDGE,{"derivedFrom":makeQuery(id+"F4.opExtrude","SWEPT_EDGE",EDGE,{"disambiguationData":[OSD([sQuery(id+"F3.wireOp",EDGE,"E25"),sQuery(id+"F3.wireOp",EDGE,"E37.trimOffspring")])]})});
            var Q93;
            Q93=makeQuery(id+"F5.boolean.opBoolean","COPY",EDGE,{"derivedFrom":makeQuery(id+"F5.opExtrude","SWEPT_EDGE",EDGE,{"disambiguationData":[OSD([sQuery(id+"F3.wireOp",EDGE,"E23"),sQuery(id+"F3.wireOp",EDGE,"E35.trimOffspring")])]})});
            var Q94;
            Q94=makeQuery(id+"F4.boolean.opBoolean","COPY",EDGE,{"derivedFrom":makeQuery(id+"F4.opExtrude","SWEPT_EDGE",EDGE,{"disambiguationData":[OSD([sQuery(id+"F3.wireOp",EDGE,"E21"),sQuery(id+"F3.wireOp",EDGE,"E36.trimOffspring")])]})});
            var Q95;
            Q95=makeQuery(id+"F4.boolean.opBoolean","COPY",EDGE,{"derivedFrom":makeQuery(id+"F4.opExtrude","SWEPT_EDGE",EDGE,{"disambiguationData":[OSD([sQuery(id+"F3.wireOp",EDGE,"E19"),sQuery(id+"F3.wireOp",EDGE,"E32.trimOffspring")])]})});
            fillet(context, id + "F6", {"entities" : qUnion([Q0, Q1, Q2, Q3, Q4, Q5, Q6, Q7, Q8, Q9, Q10, Q11, Q12, Q13, Q14, Q15, Q16, Q17, Q18, Q19, Q20, Q21, Q22, Q23, Q24, Q25, Q26, Q27, Q28, Q29, Q30, Q31, Q32, Q33, Q34, Q35, Q36, Q37, Q38, Q39, Q40, Q41, Q42, Q43, Q44, Q45, Q46, Q47, Q48, Q49, Q50, Q51, Q52, Q53, Q54, Q55, Q56, Q57, Q58, Q59, Q60, Q61, Q62, Q63, Q64, Q65, Q66, Q67, Q68, Q69, Q70, Q71, Q72, Q73, Q74, Q75, Q76, Q77, Q78, Q79, Q80, Q81, Q82, Q83, Q84, Q85, Q86, Q87, Q88, Q89, Q90, Q91, Q92, Q93, Q94, Q95]), "radius" : 2 * mm, "tangentPropagation" : true, "allowEdgeOverflow" : false});
        }
    });
